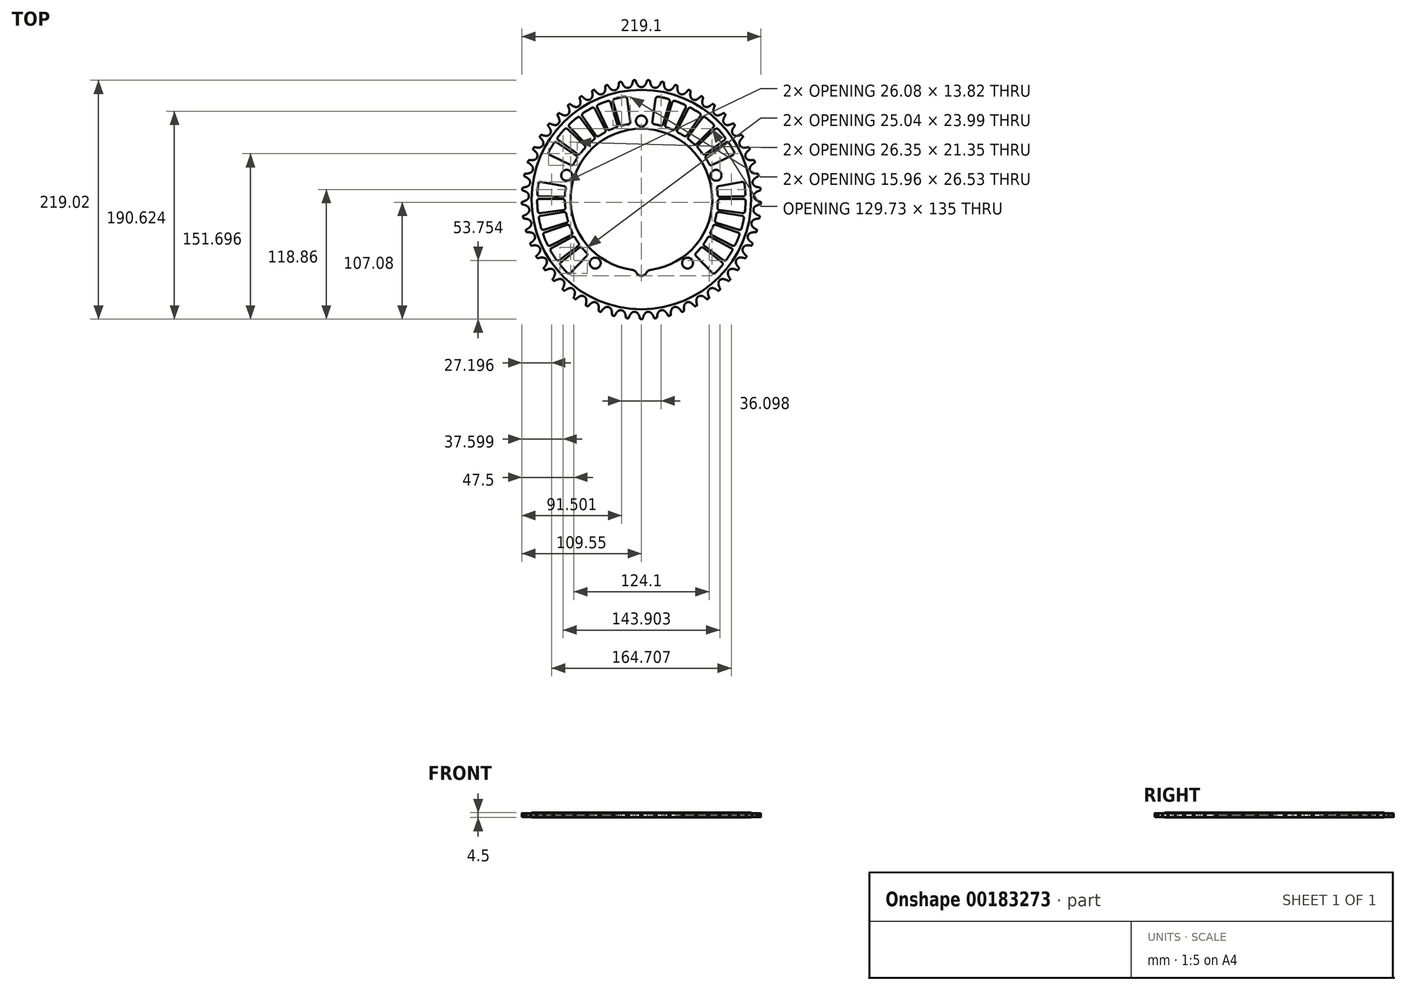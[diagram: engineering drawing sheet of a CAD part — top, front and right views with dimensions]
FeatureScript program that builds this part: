
annotation { "Feature Type Name" : "Feature", "Feature Type Description" : "" }
export const myFeature = defineFeature(function(context is Context, id is Id, definition is map)
    precondition{}
    {
        {
            var Q0;
            Q0=qCreatedBy(makeId("Top.planeOp"),FACE);
            var sketch = newSketch(context, id + "F0", { "sketchPlane" : qUnion([Q0])});
            skArc(sketch, "E0", {"start": v(-4.68, 107.46) * mm, "mid": v(-4.06, 106.06) * mm, "end": v(-3.24, 104.76) * mm});
            skLineSegment(sketch, "E1", {"start": v(-4.68, 107.46) * mm, "end": v(-5.07, 108.57) * mm});
            skArc(sketch, "E2", {"start": v(-5.07, 108.57) * mm, "mid": v(-5.69, 109.87) * mm, "end": v(-6.59, 111) * mm});
            skArc(sketch, "E3.trimOffspring", {"start": v(-3.24, 104.76) * mm, "mid": v(-1.82, 103.55) * mm, "end": v(0, 103.11) * mm});
            skArc(sketch, "E4.MirrorCS", {"start": v(3.24, 104.76) * mm, "mid": v(1.82, 103.55) * mm, "end": v(0, 103.11) * mm});
            skArc(sketch, "E5.MirrorCS", {"start": v(4.68, 107.46) * mm, "mid": v(4.06, 106.06) * mm, "end": v(3.24, 104.76) * mm});
            skLineSegment(sketch, "E6.MirrorCS", {"start": v(4.68, 107.46) * mm, "end": v(5.07, 108.57) * mm});
            skArc(sketch, "E7.MirrorCS", {"start": v(5.07, 108.57) * mm, "mid": v(5.69, 109.87) * mm, "end": v(6.59, 111) * mm});
            skCircle(sketch, "E8", {"center": v(0, 72) * mm, "radius": 5 * mm});
            skCircle(sketch, "E9", {"center": v(0, 0) * mm, "radius": 100.61 * mm});
            skCircle(sketch, "E10", {"center": v(0, 0) * mm, "radius": 65 * mm});
            skCircle(sketch, "E11.1.0", {"center": v(-68.48, 22.25) * mm, "radius": 5 * mm});
            skCircle(sketch, "E11.2.0", {"center": v(-42.32, -58.25) * mm, "radius": 5 * mm});
            skCircle(sketch, "E11.3.0", {"center": v(42.32, -58.25) * mm, "radius": 5 * mm});
            skCircle(sketch, "E11.4.0", {"center": v(68.48, 22.25) * mm, "radius": 5 * mm});
            skCircle(sketch, "E12", {"center": v(0, -65) * mm, "radius": 5 * mm});
            skArc(sketch, "E13.1.0", {"start": v(-17.87, 107.21) * mm, "mid": v(-18.64, 108.43) * mm, "end": v(-19.67, 109.44) * mm});
            skLineSegment(sketch, "E13.1.1", {"start": v(-17.36, 106.15) * mm, "end": v(-17.87, 107.21) * mm});
            skArc(sketch, "E13.1.2", {"start": v(-17.36, 106.15) * mm, "mid": v(-16.58, 104.83) * mm, "end": v(-15.61, 103.64) * mm});
            skArc(sketch, "E13.1.3", {"start": v(-15.61, 103.64) * mm, "mid": v(-14.05, 102.6) * mm, "end": v(-12.2, 102.39) * mm});
            skArc(sketch, "E13.1.4", {"start": v(-9.17, 104.4) * mm, "mid": v(-10.44, 103.04) * mm, "end": v(-12.2, 102.39) * mm});
            skArc(sketch, "E13.1.5", {"start": v(-8.06, 107.26) * mm, "mid": v(-8.51, 105.8) * mm, "end": v(-9.17, 104.4) * mm});
            skLineSegment(sketch, "E13.1.6", {"start": v(-8.06, 107.26) * mm, "end": v(-7.81, 108.4) * mm});
            skArc(sketch, "E13.1.7", {"start": v(-7.81, 108.4) * mm, "mid": v(-7.35, 109.77) * mm, "end": v(-6.59, 111) * mm});
            skArc(sketch, "E13.2.0", {"start": v(-30.43, 104.34) * mm, "mid": v(-31.34, 105.46) * mm, "end": v(-32.47, 106.34) * mm});
            skLineSegment(sketch, "E13.2.1", {"start": v(-29.79, 103.36) * mm, "end": v(-30.43, 104.34) * mm});
            skArc(sketch, "E13.2.2", {"start": v(-29.79, 103.36) * mm, "mid": v(-28.86, 102.14) * mm, "end": v(-27.76, 101.07) * mm});
            skArc(sketch, "E13.2.3", {"start": v(-27.76, 101.07) * mm, "mid": v(-26.09, 100.22) * mm, "end": v(-24.22, 100.23) * mm});
            skArc(sketch, "E13.2.4", {"start": v(-21.45, 102.6) * mm, "mid": v(-22.55, 101.08) * mm, "end": v(-24.22, 100.23) * mm});
            skArc(sketch, "E13.2.5", {"start": v(-20.7, 105.55) * mm, "mid": v(-20.96, 104.04) * mm, "end": v(-21.45, 102.6) * mm});
            skLineSegment(sketch, "E13.2.6", {"start": v(-20.7, 105.55) * mm, "end": v(-20.58, 106.72) * mm});
            skArc(sketch, "E13.2.7", {"start": v(-20.58, 106.72) * mm, "mid": v(-20.28, 108.13) * mm, "end": v(-19.67, 109.44) * mm});
            skArc(sketch, "E13.3.0", {"start": v(-42.55, 100.01) * mm, "mid": v(-43.59, 101.01) * mm, "end": v(-44.82, 101.76) * mm});
            skLineSegment(sketch, "E13.3.1", {"start": v(-41.8, 99.1) * mm, "end": v(-42.55, 100.01) * mm});
            skArc(sketch, "E13.3.2", {"start": v(-41.8, 99.1) * mm, "mid": v(-40.74, 98) * mm, "end": v(-39.52, 97.07) * mm});
            skArc(sketch, "E13.3.3", {"start": v(-39.52, 97.07) * mm, "mid": v(-37.76, 96.43) * mm, "end": v(-35.9, 96.66) * mm});
            skArc(sketch, "E13.3.4", {"start": v(-33.44, 99.33) * mm, "mid": v(-34.35, 97.7) * mm, "end": v(-35.9, 96.66) * mm});
            skArc(sketch, "E13.3.5", {"start": v(-33.03, 102.37) * mm, "mid": v(-33.12, 100.83) * mm, "end": v(-33.44, 99.33) * mm});
            skLineSegment(sketch, "E13.3.6", {"start": v(-33.03, 102.37) * mm, "end": v(-33.06, 103.54) * mm});
            skArc(sketch, "E13.3.7", {"start": v(-33.06, 103.54) * mm, "mid": v(-32.92, 104.98) * mm, "end": v(-32.47, 106.34) * mm});
            skArc(sketch, "E13.4.0", {"start": v(-54.08, 94.28) * mm, "mid": v(-55.23, 95.15) * mm, "end": v(-56.54, 95.74) * mm});
            skLineSegment(sketch, "E13.4.1", {"start": v(-53.23, 93.47) * mm, "end": v(-54.08, 94.28) * mm});
            skArc(sketch, "E13.4.2", {"start": v(-53.23, 93.47) * mm, "mid": v(-52.04, 92.5) * mm, "end": v(-50.72, 91.72) * mm});
            skArc(sketch, "E13.4.3", {"start": v(-50.72, 91.72) * mm, "mid": v(-48.9, 91.3) * mm, "end": v(-47.08, 91.73) * mm});
            skArc(sketch, "E13.4.4", {"start": v(-44.95, 94.68) * mm, "mid": v(-45.66, 92.95) * mm, "end": v(-47.08, 91.73) * mm});
            skArc(sketch, "E13.4.5", {"start": v(-44.9, 97.74) * mm, "mid": v(-44.82, 96.2) * mm, "end": v(-44.95, 94.68) * mm});
            skLineSegment(sketch, "E13.4.6", {"start": v(-44.9, 97.74) * mm, "end": v(-45.07, 98.9) * mm});
            skArc(sketch, "E13.4.7", {"start": v(-45.07, 98.9) * mm, "mid": v(-45.1, 100.34) * mm, "end": v(-44.82, 101.76) * mm});
            skArc(sketch, "E13.5.0", {"start": v(-64.85, 87.22) * mm, "mid": v(-66.1, 87.95) * mm, "end": v(-67.47, 88.38) * mm});
            skLineSegment(sketch, "E13.5.1", {"start": v(-63.91, 86.52) * mm, "end": v(-64.85, 87.22) * mm});
            skArc(sketch, "E13.5.2", {"start": v(-63.91, 86.52) * mm, "mid": v(-62.62, 85.7) * mm, "end": v(-61.21, 85.08) * mm});
            skArc(sketch, "E13.5.3", {"start": v(-61.21, 85.08) * mm, "mid": v(-59.35, 84.87) * mm, "end": v(-57.6, 85.52) * mm});
            skArc(sketch, "E13.5.4", {"start": v(-55.83, 88.7) * mm, "mid": v(-56.34, 86.9) * mm, "end": v(-57.6, 85.52) * mm});
            skArc(sketch, "E13.5.5", {"start": v(-56.15, 91.74) * mm, "mid": v(-55.88, 90.23) * mm, "end": v(-55.83, 88.7) * mm});
            skLineSegment(sketch, "E13.5.6", {"start": v(-56.15, 91.74) * mm, "end": v(-56.45, 92.88) * mm});
            skArc(sketch, "E13.5.7", {"start": v(-56.45, 92.88) * mm, "mid": v(-56.66, 94.3) * mm, "end": v(-56.54, 95.74) * mm});
            skArc(sketch, "E13.6.0", {"start": v(-74.72, 78.94) * mm, "mid": v(-76.04, 79.51) * mm, "end": v(-77.45, 79.78) * mm});
            skLineSegment(sketch, "E13.6.1", {"start": v(-73.7, 78.35) * mm, "end": v(-74.72, 78.94) * mm});
            skArc(sketch, "E13.6.2", {"start": v(-73.7, 78.35) * mm, "mid": v(-72.31, 77.69) * mm, "end": v(-70.85, 77.24) * mm});
            skArc(sketch, "E13.6.3", {"start": v(-70.85, 77.24) * mm, "mid": v(-68.98, 77.25) * mm, "end": v(-67.31, 78.1) * mm});
            skArc(sketch, "E13.6.4", {"start": v(-65.93, 81.47) * mm, "mid": v(-66.22, 79.63) * mm, "end": v(-67.31, 78.1) * mm});
            skArc(sketch, "E13.6.5", {"start": v(-66.6, 84.46) * mm, "mid": v(-66.16, 83) * mm, "end": v(-65.93, 81.47) * mm});
            skLineSegment(sketch, "E13.6.6", {"start": v(-66.6, 84.46) * mm, "end": v(-67.04, 85.55) * mm});
            skArc(sketch, "E13.6.7", {"start": v(-67.04, 85.55) * mm, "mid": v(-67.42, 86.94) * mm, "end": v(-67.47, 88.38) * mm});
            skArc(sketch, "E13.7.0", {"start": v(-83.53, 69.55) * mm, "mid": v(-84.9, 69.96) * mm, "end": v(-86.34, 70.06) * mm});
            skLineSegment(sketch, "E13.7.1", {"start": v(-82.45, 69.08) * mm, "end": v(-83.53, 69.55) * mm});
            skArc(sketch, "E13.7.2", {"start": v(-82.45, 69.08) * mm, "mid": v(-81, 68.6) * mm, "end": v(-79.48, 68.32) * mm});
            skArc(sketch, "E13.7.3", {"start": v(-79.48, 68.32) * mm, "mid": v(-77.63, 68.55) * mm, "end": v(-76.08, 69.6) * mm});
            skArc(sketch, "E13.7.4", {"start": v(-75.1, 73.1) * mm, "mid": v(-75.17, 71.23) * mm, "end": v(-76.08, 69.6) * mm});
            skArc(sketch, "E13.7.5", {"start": v(-76.13, 75.99) * mm, "mid": v(-75.51, 74.58) * mm, "end": v(-75.1, 73.1) * mm});
            skLineSegment(sketch, "E13.7.6", {"start": v(-76.13, 75.99) * mm, "end": v(-76.69, 77.02) * mm});
            skArc(sketch, "E13.7.7", {"start": v(-76.69, 77.02) * mm, "mid": v(-77.23, 78.36) * mm, "end": v(-77.45, 79.78) * mm});
            skArc(sketch, "E13.8.0", {"start": v(-91.17, 59.18) * mm, "mid": v(-92.58, 59.43) * mm, "end": v(-94.02, 59.36) * mm});
            skLineSegment(sketch, "E13.8.1", {"start": v(-90.04, 58.85) * mm, "end": v(-91.17, 59.18) * mm});
            skArc(sketch, "E13.8.2", {"start": v(-90.04, 58.85) * mm, "mid": v(-88.54, 58.53) * mm, "end": v(-87, 58.44) * mm});
            skArc(sketch, "E13.8.3", {"start": v(-87, 58.44) * mm, "mid": v(-85.2, 58.89) * mm, "end": v(-83.78, 60.11) * mm});
            skArc(sketch, "E13.8.4", {"start": v(-83.23, 63.7) * mm, "mid": v(-83.07, 61.84) * mm, "end": v(-83.78, 60.11) * mm});
            skArc(sketch, "E13.8.5", {"start": v(-84.58, 66.45) * mm, "mid": v(-83.8, 65.13) * mm, "end": v(-83.23, 63.7) * mm});
            skLineSegment(sketch, "E13.8.6", {"start": v(-84.58, 66.45) * mm, "end": v(-85.26, 67.41) * mm});
            skArc(sketch, "E13.8.7", {"start": v(-85.26, 67.41) * mm, "mid": v(-85.95, 68.67) * mm, "end": v(-86.34, 70.06) * mm});
            skArc(sketch, "E13.9.0", {"start": v(-97.53, 47.98) * mm, "mid": v(-98.96, 48.06) * mm, "end": v(-100.38, 47.82) * mm});
            skLineSegment(sketch, "E13.9.1", {"start": v(-96.37, 47.78) * mm, "end": v(-97.53, 47.98) * mm});
            skArc(sketch, "E13.9.2", {"start": v(-96.37, 47.78) * mm, "mid": v(-94.84, 47.65) * mm, "end": v(-93.3, 47.74) * mm});
            skArc(sketch, "E13.9.3", {"start": v(-93.3, 47.74) * mm, "mid": v(-91.56, 48.4) * mm, "end": v(-90.3, 49.78) * mm});
            skArc(sketch, "E13.9.4", {"start": v(-90.18, 53.42) * mm, "mid": v(-89.8, 51.58) * mm, "end": v(-90.3, 49.78) * mm});
            skArc(sketch, "E13.9.5", {"start": v(-91.85, 55.98) * mm, "mid": v(-90.92, 54.76) * mm, "end": v(-90.18, 53.42) * mm});
            skLineSegment(sketch, "E13.9.6", {"start": v(-91.85, 55.98) * mm, "end": v(-92.63, 56.85) * mm});
            skArc(sketch, "E13.9.7", {"start": v(-92.63, 56.85) * mm, "mid": v(-93.47, 58.03) * mm, "end": v(-94.02, 59.36) * mm});
            skArc(sketch, "E13.10.0", {"start": v(-102.52, 36.11) * mm, "mid": v(-103.95, 36.02) * mm, "end": v(-105.33, 35.61) * mm});
            skLineSegment(sketch, "E13.10.1", {"start": v(-101.34, 36.05) * mm, "end": v(-102.52, 36.11) * mm});
            skArc(sketch, "E13.10.2", {"start": v(-101.34, 36.05) * mm, "mid": v(-99.8, 36.1) * mm, "end": v(-98.3, 36.37) * mm});
            skArc(sketch, "E13.10.3", {"start": v(-98.3, 36.37) * mm, "mid": v(-96.64, 37.23) * mm, "end": v(-95.55, 38.75) * mm});
            skArc(sketch, "E13.10.4", {"start": v(-95.86, 42.38) * mm, "mid": v(-95.27, 40.6) * mm, "end": v(-95.55, 38.75) * mm});
            skArc(sketch, "E13.10.5", {"start": v(-97.82, 44.72) * mm, "mid": v(-96.76, 43.62) * mm, "end": v(-95.86, 42.38) * mm});
            skLineSegment(sketch, "E13.10.6", {"start": v(-97.82, 44.72) * mm, "end": v(-98.7, 45.5) * mm});
            skArc(sketch, "E13.10.7", {"start": v(-98.7, 45.5) * mm, "mid": v(-99.68, 46.56) * mm, "end": v(-100.38, 47.82) * mm});
            skArc(sketch, "E13.11.0", {"start": v(-106.07, 23.73) * mm, "mid": v(-107.48, 23.47) * mm, "end": v(-108.8, 22.9) * mm});
            skLineSegment(sketch, "E13.11.1", {"start": v(-104.9, 23.81) * mm, "end": v(-106.07, 23.73) * mm});
            skArc(sketch, "E13.11.2", {"start": v(-104.9, 23.81) * mm, "mid": v(-103.38, 24.04) * mm, "end": v(-101.9, 24.49) * mm});
            skArc(sketch, "E13.11.3", {"start": v(-101.9, 24.49) * mm, "mid": v(-100.37, 25.54) * mm, "end": v(-99.47, 27.18) * mm});
            skArc(sketch, "E13.11.4", {"start": v(-100.2, 30.74) * mm, "mid": v(-99.4, 29.05) * mm, "end": v(-99.47, 27.18) * mm});
            skArc(sketch, "E13.11.5", {"start": v(-102.43, 32.84) * mm, "mid": v(-101.24, 31.87) * mm, "end": v(-100.2, 30.74) * mm});
            skLineSegment(sketch, "E13.11.6", {"start": v(-102.43, 32.84) * mm, "end": v(-103.4, 33.5) * mm});
            skArc(sketch, "E13.11.7", {"start": v(-103.4, 33.5) * mm, "mid": v(-104.49, 34.45) * mm, "end": v(-105.33, 35.61) * mm});
            skArc(sketch, "E13.12.0", {"start": v(-108.13, 11.02) * mm, "mid": v(-109.5, 10.6) * mm, "end": v(-110.75, 9.87) * mm});
            skLineSegment(sketch, "E13.12.1", {"start": v(-106.97, 11.24) * mm, "end": v(-108.13, 11.02) * mm});
            skArc(sketch, "E13.12.2", {"start": v(-106.97, 11.24) * mm, "mid": v(-105.5, 11.64) * mm, "end": v(-104.1, 12.26) * mm});
            skArc(sketch, "E13.12.3", {"start": v(-104.1, 12.26) * mm, "mid": v(-102.68, 13.49) * mm, "end": v(-101.98, 15.22) * mm});
            skArc(sketch, "E13.12.4", {"start": v(-103.13, 18.67) * mm, "mid": v(-102.14, 17.09) * mm, "end": v(-101.98, 15.22) * mm});
            skArc(sketch, "E13.12.5", {"start": v(-105.6, 20.5) * mm, "mid": v(-104.3, 19.68) * mm, "end": v(-103.13, 18.67) * mm});
            skLineSegment(sketch, "E13.12.6", {"start": v(-105.6, 20.5) * mm, "end": v(-106.63, 21.04) * mm});
            skArc(sketch, "E13.12.7", {"start": v(-106.63, 21.04) * mm, "mid": v(-107.83, 21.85) * mm, "end": v(-108.8, 22.9) * mm});
            skArc(sketch, "E13.13.0", {"start": v(-108.67, -1.85) * mm, "mid": v(-110, -2.43) * mm, "end": v(-111.14, -3.3) * mm});
            skLineSegment(sketch, "E13.13.1", {"start": v(-107.55, -1.5) * mm, "end": v(-108.67, -1.85) * mm});
            skArc(sketch, "E13.13.2", {"start": v(-107.55, -1.5) * mm, "mid": v(-106.13, -0.92) * mm, "end": v(-104.8, -0.14) * mm});
            skArc(sketch, "E13.13.3", {"start": v(-104.8, -0.14) * mm, "mid": v(-103.56, 1.25) * mm, "end": v(-103.07, 3.06) * mm});
            skArc(sketch, "E13.13.4", {"start": v(-104.62, 6.35) * mm, "mid": v(-103.45, 4.89) * mm, "end": v(-103.07, 3.06) * mm});
            skArc(sketch, "E13.13.5", {"start": v(-107.28, 7.86) * mm, "mid": v(-105.9, 7.2) * mm, "end": v(-104.62, 6.35) * mm});
            skLineSegment(sketch, "E13.13.6", {"start": v(-107.28, 7.86) * mm, "end": v(-108.37, 8.28) * mm});
            skArc(sketch, "E13.13.7", {"start": v(-108.37, 8.28) * mm, "mid": v(-109.65, 8.94) * mm, "end": v(-110.75, 9.87) * mm});
            skArc(sketch, "E13.14.0", {"start": v(-107.7, -14.69) * mm, "mid": v(-108.93, -15.42) * mm, "end": v(-109.97, -16.42) * mm});
            skLineSegment(sketch, "E13.14.1", {"start": v(-106.62, -14.2) * mm, "end": v(-107.7, -14.69) * mm});
            skArc(sketch, "E13.14.2", {"start": v(-106.62, -14.2) * mm, "mid": v(-105.28, -13.46) * mm, "end": v(-104.06, -12.53) * mm});
            skArc(sketch, "E13.14.3", {"start": v(-104.06, -12.53) * mm, "mid": v(-102.98, -11) * mm, "end": v(-102.7, -9.16) * mm});
            skArc(sketch, "E13.14.4", {"start": v(-104.63, -6.07) * mm, "mid": v(-103.3, -7.38) * mm, "end": v(-102.7, -9.16) * mm});
            skArc(sketch, "E13.14.5", {"start": v(-107.45, -4.88) * mm, "mid": v(-106, -5.37) * mm, "end": v(-104.63, -6.07) * mm});
            skLineSegment(sketch, "E13.14.6", {"start": v(-107.45, -4.88) * mm, "end": v(-108.6, -4.6) * mm});
            skArc(sketch, "E13.14.7", {"start": v(-108.6, -4.6) * mm, "mid": v(-109.94, -4.09) * mm, "end": v(-111.14, -3.3) * mm});
            skArc(sketch, "E13.15.0", {"start": v(-105.2, -27.32) * mm, "mid": v(-106.34, -28.2) * mm, "end": v(-107.26, -29.3) * mm});
            skLineSegment(sketch, "E13.15.1", {"start": v(-104.2, -26.71) * mm, "end": v(-105.2, -27.32) * mm});
            skArc(sketch, "E13.15.2", {"start": v(-104.2, -26.71) * mm, "mid": v(-102.95, -25.82) * mm, "end": v(-101.85, -24.75) * mm});
            skArc(sketch, "E13.15.3", {"start": v(-101.85, -24.75) * mm, "mid": v(-100.95, -23.1) * mm, "end": v(-100.9, -21.24) * mm});
            skArc(sketch, "E13.15.4", {"start": v(-103.18, -18.4) * mm, "mid": v(-101.7, -19.55) * mm, "end": v(-100.9, -21.24) * mm});
            skArc(sketch, "E13.15.5", {"start": v(-106.12, -17.56) * mm, "mid": v(-104.62, -17.87) * mm, "end": v(-103.18, -18.4) * mm});
            skLineSegment(sketch, "E13.15.6", {"start": v(-106.12, -17.56) * mm, "end": v(-107.29, -17.4) * mm});
            skArc(sketch, "E13.15.7", {"start": v(-107.29, -17.4) * mm, "mid": v(-108.69, -17.06) * mm, "end": v(-109.97, -16.42) * mm});
            skArc(sketch, "E13.16.0", {"start": v(-101.23, -39.57) * mm, "mid": v(-102.26, -40.58) * mm, "end": v(-103.04, -41.79) * mm});
            skLineSegment(sketch, "E13.16.1", {"start": v(-100.3, -38.85) * mm, "end": v(-101.23, -39.57) * mm});
            skArc(sketch, "E13.16.2", {"start": v(-100.3, -38.85) * mm, "mid": v(-99.17, -37.81) * mm, "end": v(-98.2, -36.62) * mm});
            skArc(sketch, "E13.16.3", {"start": v(-98.2, -36.62) * mm, "mid": v(-97.51, -34.89) * mm, "end": v(-97.68, -33.02) * mm});
            skArc(sketch, "E13.16.4", {"start": v(-100.28, -30.48) * mm, "mid": v(-98.68, -31.44) * mm, "end": v(-97.68, -33.02) * mm});
            skArc(sketch, "E13.16.5", {"start": v(-103.3, -29.98) * mm, "mid": v(-101.77, -30.12) * mm, "end": v(-100.28, -30.48) * mm});
            skLineSegment(sketch, "E13.16.6", {"start": v(-103.3, -29.98) * mm, "end": v(-104.48, -29.97) * mm});
            skArc(sketch, "E13.16.7", {"start": v(-104.48, -29.97) * mm, "mid": v(-105.9, -29.8) * mm, "end": v(-107.26, -29.3) * mm});
            skArc(sketch, "E13.17.0", {"start": v(-95.84, -51.27) * mm, "mid": v(-96.74, -52.39) * mm, "end": v(-97.37, -53.68) * mm});
            skLineSegment(sketch, "E13.17.1", {"start": v(-95, -50.44) * mm, "end": v(-95.84, -51.27) * mm});
            skArc(sketch, "E13.17.2", {"start": v(-95, -50.44) * mm, "mid": v(-94, -49.28) * mm, "end": v(-93.18, -47.98) * mm});
            skArc(sketch, "E13.17.3", {"start": v(-93.18, -47.98) * mm, "mid": v(-92.7, -46.17) * mm, "end": v(-93.09, -44.34) * mm});
            skArc(sketch, "E13.17.4", {"start": v(-95.97, -42.13) * mm, "mid": v(-94.26, -42.9) * mm, "end": v(-93.09, -44.34) * mm});
            skArc(sketch, "E13.17.5", {"start": v(-99.03, -42) * mm, "mid": v(-97.5, -41.95) * mm, "end": v(-95.97, -42.13) * mm});
            skLineSegment(sketch, "E13.17.6", {"start": v(-99.03, -42) * mm, "end": v(-100.2, -42.12) * mm});
            skArc(sketch, "E13.17.7", {"start": v(-100.2, -42.12) * mm, "mid": v(-101.64, -42.12) * mm, "end": v(-103.04, -41.79) * mm});
            skArc(sketch, "E13.18.0", {"start": v(-89.1, -62.24) * mm, "mid": v(-89.87, -63.46) * mm, "end": v(-90.34, -64.82) * mm});
            skLineSegment(sketch, "E13.18.1", {"start": v(-88.37, -61.32) * mm, "end": v(-89.1, -62.24) * mm});
            skArc(sketch, "E13.18.2", {"start": v(-88.37, -61.32) * mm, "mid": v(-87.51, -60.05) * mm, "end": v(-86.85, -58.67) * mm});
            skArc(sketch, "E13.18.3", {"start": v(-86.85, -58.67) * mm, "mid": v(-86.59, -56.81) * mm, "end": v(-87.2, -55.04) * mm});
            skArc(sketch, "E13.18.4", {"start": v(-90.32, -53.18) * mm, "mid": v(-88.53, -53.74) * mm, "end": v(-87.2, -55.04) * mm});
            skArc(sketch, "E13.18.5", {"start": v(-93.37, -53.4) * mm, "mid": v(-91.85, -53.18) * mm, "end": v(-90.32, -53.18) * mm});
            skLineSegment(sketch, "E13.18.6", {"start": v(-93.37, -53.4) * mm, "end": v(-94.51, -53.67) * mm});
            skArc(sketch, "E13.18.7", {"start": v(-94.51, -53.67) * mm, "mid": v(-95.94, -53.84) * mm, "end": v(-97.37, -53.68) * mm});
            skArc(sketch, "E13.19.0", {"start": v(-81.12, -72.34) * mm, "mid": v(-81.73, -73.65) * mm, "end": v(-82.04, -75.05) * mm});
            skLineSegment(sketch, "E13.19.1", {"start": v(-80.5, -71.34) * mm, "end": v(-81.12, -72.34) * mm});
            skArc(sketch, "E13.19.2", {"start": v(-80.5, -71.34) * mm, "mid": v(-79.8, -69.98) * mm, "end": v(-79.3, -68.53) * mm});
            skArc(sketch, "E13.19.3", {"start": v(-79.3, -68.53) * mm, "mid": v(-79.26, -66.66) * mm, "end": v(-80.07, -64.97) * mm});
            skArc(sketch, "E13.19.4", {"start": v(-83.4, -63.49) * mm, "mid": v(-81.55, -63.83) * mm, "end": v(-80.07, -64.97) * mm});
            skArc(sketch, "E13.19.5", {"start": v(-86.4, -64.08) * mm, "mid": v(-84.91, -63.67) * mm, "end": v(-83.4, -63.49) * mm});
            skLineSegment(sketch, "E13.19.6", {"start": v(-86.4, -64.08) * mm, "end": v(-87.5, -64.48) * mm});
            skArc(sketch, "E13.19.7", {"start": v(-87.5, -64.48) * mm, "mid": v(-88.9, -64.81) * mm, "end": v(-90.34, -64.82) * mm});
            skArc(sketch, "E13.20.0", {"start": v(-72, -81.43) * mm, "mid": v(-72.45, -82.8) * mm, "end": v(-72.59, -84.23) * mm});
            skLineSegment(sketch, "E13.20.1", {"start": v(-71.5, -80.36) * mm, "end": v(-72, -81.43) * mm});
            skArc(sketch, "E13.20.2", {"start": v(-71.5, -80.36) * mm, "mid": v(-70.96, -78.93) * mm, "end": v(-70.64, -77.42) * mm});
            skArc(sketch, "E13.20.3", {"start": v(-70.64, -77.42) * mm, "mid": v(-70.82, -75.56) * mm, "end": v(-71.82, -73.98) * mm});
            skArc(sketch, "E13.20.4", {"start": v(-75.3, -72.9) * mm, "mid": v(-73.43, -73.03) * mm, "end": v(-71.82, -73.98) * mm});
            skArc(sketch, "E13.20.5", {"start": v(-78.2, -73.85) * mm, "mid": v(-76.79, -73.27) * mm, "end": v(-75.3, -72.9) * mm});
            skLineSegment(sketch, "E13.20.6", {"start": v(-78.2, -73.85) * mm, "end": v(-79.26, -74.37) * mm});
            skArc(sketch, "E13.20.7", {"start": v(-79.26, -74.37) * mm, "mid": v(-80.61, -74.87) * mm, "end": v(-82.04, -75.05) * mm});
            skArc(sketch, "E13.21.0", {"start": v(-61.86, -89.37) * mm, "mid": v(-62.15, -90.78) * mm, "end": v(-62.12, -92.22) * mm});
            skLineSegment(sketch, "E13.21.1", {"start": v(-61.49, -88.26) * mm, "end": v(-61.86, -89.37) * mm});
            skArc(sketch, "E13.21.2", {"start": v(-61.49, -88.26) * mm, "mid": v(-61.13, -86.76) * mm, "end": v(-61, -85.24) * mm});
            skArc(sketch, "E13.21.3", {"start": v(-61, -85.24) * mm, "mid": v(-61.39, -83.4) * mm, "end": v(-62.57, -81.96) * mm});
            skArc(sketch, "E13.21.4", {"start": v(-66.15, -81.3) * mm, "mid": v(-64.28, -81.2) * mm, "end": v(-62.57, -81.96) * mm});
            skArc(sketch, "E13.21.5", {"start": v(-68.93, -82.58) * mm, "mid": v(-67.58, -81.84) * mm, "end": v(-66.15, -81.3) * mm});
            skLineSegment(sketch, "E13.21.6", {"start": v(-68.93, -82.58) * mm, "end": v(-69.9, -83.23) * mm});
            skArc(sketch, "E13.21.7", {"start": v(-69.9, -83.23) * mm, "mid": v(-71.2, -83.88) * mm, "end": v(-72.59, -84.23) * mm});
            skArc(sketch, "E13.22.0", {"start": v(-50.85, -96.06) * mm, "mid": v(-50.97, -97.5) * mm, "end": v(-50.77, -98.92) * mm});
            skLineSegment(sketch, "E13.22.1", {"start": v(-50.62, -94.9) * mm, "end": v(-50.85, -96.06) * mm});
            skArc(sketch, "E13.22.2", {"start": v(-50.62, -94.9) * mm, "mid": v(-50.44, -93.39) * mm, "end": v(-50.48, -91.85) * mm});
            skArc(sketch, "E13.22.3", {"start": v(-50.48, -91.85) * mm, "mid": v(-51.1, -90.08) * mm, "end": v(-52.44, -88.78) * mm});
            skArc(sketch, "E13.22.4", {"start": v(-56.07, -88.55) * mm, "mid": v(-54.22, -88.23) * mm, "end": v(-52.44, -88.78) * mm});
            skArc(sketch, "E13.22.5", {"start": v(-58.68, -90.15) * mm, "mid": v(-57.43, -89.25) * mm, "end": v(-56.07, -88.55) * mm});
            skLineSegment(sketch, "E13.22.6", {"start": v(-58.68, -90.15) * mm, "end": v(-59.57, -90.9) * mm});
            skArc(sketch, "E13.22.7", {"start": v(-59.57, -90.9) * mm, "mid": v(-60.77, -91.71) * mm, "end": v(-62.12, -92.22) * mm});
            skArc(sketch, "E13.23.0", {"start": v(-39.13, -101.4) * mm, "mid": v(-39.09, -102.84) * mm, "end": v(-38.72, -104.23) * mm});
            skLineSegment(sketch, "E13.23.1", {"start": v(-39.04, -100.23) * mm, "end": v(-39.13, -101.4) * mm});
            skArc(sketch, "E13.23.2", {"start": v(-39.04, -100.23) * mm, "mid": v(-39.04, -98.7) * mm, "end": v(-39.26, -97.18) * mm});
            skArc(sketch, "E13.23.3", {"start": v(-39.26, -97.18) * mm, "mid": v(-40.08, -95.5) * mm, "end": v(-41.57, -94.36) * mm});
            skArc(sketch, "E13.23.4", {"start": v(-45.2, -94.56) * mm, "mid": v(-43.4, -94.03) * mm, "end": v(-41.57, -94.36) * mm});
            skArc(sketch, "E13.23.5", {"start": v(-47.6, -96.46) * mm, "mid": v(-46.47, -95.42) * mm, "end": v(-45.2, -94.56) * mm});
            skLineSegment(sketch, "E13.23.6", {"start": v(-47.6, -96.46) * mm, "end": v(-48.4, -97.32) * mm});
            skArc(sketch, "E13.23.7", {"start": v(-48.4, -97.32) * mm, "mid": v(-49.5, -98.25) * mm, "end": v(-50.77, -98.92) * mm});
            skArc(sketch, "E13.24.0", {"start": v(-26.86, -105.32) * mm, "mid": v(-26.65, -106.74) * mm, "end": v(-26.12, -108.08) * mm});
            skLineSegment(sketch, "E13.24.1", {"start": v(-26.9, -104.14) * mm, "end": v(-26.86, -105.32) * mm});
            skArc(sketch, "E13.24.2", {"start": v(-26.9, -104.14) * mm, "mid": v(-27.1, -102.62) * mm, "end": v(-27.5, -101.14) * mm});
            skArc(sketch, "E13.24.3", {"start": v(-27.5, -101.14) * mm, "mid": v(-28.5, -99.56) * mm, "end": v(-30.11, -98.62) * mm});
            skArc(sketch, "E13.24.4", {"start": v(-33.7, -99.25) * mm, "mid": v(-31.98, -98.5) * mm, "end": v(-30.11, -98.62) * mm});
            skArc(sketch, "E13.24.5", {"start": v(-35.86, -101.4) * mm, "mid": v(-34.86, -100.25) * mm, "end": v(-33.7, -99.25) * mm});
            skLineSegment(sketch, "E13.24.6", {"start": v(-35.86, -101.4) * mm, "end": v(-36.55, -102.36) * mm});
            skArc(sketch, "E13.24.7", {"start": v(-36.55, -102.36) * mm, "mid": v(-37.53, -103.42) * mm, "end": v(-38.72, -104.23) * mm});
            skArc(sketch, "E13.25.0", {"start": v(-14.22, -107.76) * mm, "mid": v(-13.84, -109.14) * mm, "end": v(-13.15, -110.41) * mm});
            skLineSegment(sketch, "E13.25.1", {"start": v(-14.4, -106.6) * mm, "end": v(-14.22, -107.76) * mm});
            skArc(sketch, "E13.25.2", {"start": v(-14.4, -106.6) * mm, "mid": v(-14.76, -105.1) * mm, "end": v(-15.34, -103.68) * mm});
            skArc(sketch, "E13.25.3", {"start": v(-15.34, -103.68) * mm, "mid": v(-16.53, -102.24) * mm, "end": v(-18.24, -101.49) * mm});
            skArc(sketch, "E13.25.4", {"start": v(-21.72, -102.53) * mm, "mid": v(-20.1, -101.6) * mm, "end": v(-18.24, -101.49) * mm});
            skArc(sketch, "E13.25.5", {"start": v(-23.61, -104.94) * mm, "mid": v(-22.76, -103.67) * mm, "end": v(-21.72, -102.53) * mm});
            skLineSegment(sketch, "E13.25.6", {"start": v(-23.61, -104.94) * mm, "end": v(-24.2, -105.96) * mm});
            skArc(sketch, "E13.25.7", {"start": v(-24.2, -105.96) * mm, "mid": v(-25.03, -107.13) * mm, "end": v(-26.12, -108.08) * mm});
            skArc(sketch, "E13.26.0", {"start": v(-1.38, -108.68) * mm, "mid": v(-0.83, -110.01) * mm, "end": v(0, -111.2) * mm});
            skLineSegment(sketch, "E13.26.1", {"start": v(-1.7, -107.55) * mm, "end": v(-1.38, -108.68) * mm});
            skArc(sketch, "E13.26.2", {"start": v(-1.7, -107.55) * mm, "mid": v(-2.23, -106.11) * mm, "end": v(-2.97, -104.77) * mm});
            skArc(sketch, "E13.26.3", {"start": v(-2.97, -104.77) * mm, "mid": v(-4.32, -103.47) * mm, "end": v(-6.1, -102.93) * mm});
            skArc(sketch, "E13.26.4", {"start": v(-9.44, -104.38) * mm, "mid": v(-7.95, -103.26) * mm, "end": v(-6.1, -102.93) * mm});
            skArc(sketch, "E13.26.5", {"start": v(-11.04, -107) * mm, "mid": v(-10.34, -105.63) * mm, "end": v(-9.44, -104.38) * mm});
            skLineSegment(sketch, "E13.26.6", {"start": v(-11.04, -107) * mm, "end": v(-11.49, -108.08) * mm});
            skArc(sketch, "E13.26.7", {"start": v(-11.49, -108.08) * mm, "mid": v(-12.19, -109.34) * mm, "end": v(-13.15, -110.41) * mm});
            skArc(sketch, "E13.27.0", {"start": v(11.49, -108.08) * mm, "mid": v(12.19, -109.34) * mm, "end": v(13.15, -110.41) * mm});
            skLineSegment(sketch, "E13.27.1", {"start": v(11.04, -107) * mm, "end": v(11.49, -108.08) * mm});
            skArc(sketch, "E13.27.2", {"start": v(11.04, -107) * mm, "mid": v(10.34, -105.63) * mm, "end": v(9.44, -104.38) * mm});
            skArc(sketch, "E13.27.3", {"start": v(9.44, -104.38) * mm, "mid": v(7.95, -103.26) * mm, "end": v(6.1, -102.93) * mm});
            skArc(sketch, "E13.27.4", {"start": v(2.97, -104.77) * mm, "mid": v(4.32, -103.47) * mm, "end": v(6.1, -102.93) * mm});
            skArc(sketch, "E13.27.5", {"start": v(1.7, -107.55) * mm, "mid": v(2.23, -106.11) * mm, "end": v(2.97, -104.77) * mm});
            skLineSegment(sketch, "E13.27.6", {"start": v(1.7, -107.55) * mm, "end": v(1.38, -108.68) * mm});
            skArc(sketch, "E13.27.7", {"start": v(1.38, -108.68) * mm, "mid": v(0.83, -110.01) * mm, "end": v(0, -111.2) * mm});
            skArc(sketch, "E13.28.0", {"start": v(24.2, -105.96) * mm, "mid": v(25.03, -107.13) * mm, "end": v(26.12, -108.08) * mm});
            skLineSegment(sketch, "E13.28.1", {"start": v(23.61, -104.94) * mm, "end": v(24.2, -105.96) * mm});
            skArc(sketch, "E13.28.2", {"start": v(23.61, -104.94) * mm, "mid": v(22.76, -103.67) * mm, "end": v(21.72, -102.53) * mm});
            skArc(sketch, "E13.28.3", {"start": v(21.72, -102.53) * mm, "mid": v(20.1, -101.6) * mm, "end": v(18.24, -101.49) * mm});
            skArc(sketch, "E13.28.4", {"start": v(15.34, -103.68) * mm, "mid": v(16.53, -102.24) * mm, "end": v(18.24, -101.49) * mm});
            skArc(sketch, "E13.28.5", {"start": v(14.4, -106.6) * mm, "mid": v(14.76, -105.1) * mm, "end": v(15.34, -103.68) * mm});
            skLineSegment(sketch, "E13.28.6", {"start": v(14.4, -106.6) * mm, "end": v(14.22, -107.76) * mm});
            skArc(sketch, "E13.28.7", {"start": v(14.22, -107.76) * mm, "mid": v(13.84, -109.14) * mm, "end": v(13.15, -110.41) * mm});
            skArc(sketch, "E13.29.0", {"start": v(36.55, -102.36) * mm, "mid": v(37.53, -103.42) * mm, "end": v(38.72, -104.23) * mm});
            skLineSegment(sketch, "E13.29.1", {"start": v(35.86, -101.4) * mm, "end": v(36.55, -102.36) * mm});
            skArc(sketch, "E13.29.2", {"start": v(35.86, -101.4) * mm, "mid": v(34.86, -100.25) * mm, "end": v(33.7, -99.25) * mm});
            skArc(sketch, "E13.29.3", {"start": v(33.7, -99.25) * mm, "mid": v(31.98, -98.5) * mm, "end": v(30.11, -98.62) * mm});
            skArc(sketch, "E13.29.4", {"start": v(27.5, -101.14) * mm, "mid": v(28.5, -99.56) * mm, "end": v(30.11, -98.62) * mm});
            skArc(sketch, "E13.29.5", {"start": v(26.9, -104.14) * mm, "mid": v(27.1, -102.62) * mm, "end": v(27.5, -101.14) * mm});
            skLineSegment(sketch, "E13.29.6", {"start": v(26.9, -104.14) * mm, "end": v(26.86, -105.32) * mm});
            skArc(sketch, "E13.29.7", {"start": v(26.86, -105.32) * mm, "mid": v(26.65, -106.74) * mm, "end": v(26.12, -108.08) * mm});
            skArc(sketch, "E13.30.0", {"start": v(48.4, -97.32) * mm, "mid": v(49.5, -98.25) * mm, "end": v(50.77, -98.92) * mm});
            skLineSegment(sketch, "E13.30.1", {"start": v(47.6, -96.46) * mm, "end": v(48.4, -97.32) * mm});
            skArc(sketch, "E13.30.2", {"start": v(47.6, -96.46) * mm, "mid": v(46.47, -95.42) * mm, "end": v(45.2, -94.56) * mm});
            skArc(sketch, "E13.30.3", {"start": v(45.2, -94.56) * mm, "mid": v(43.4, -94.03) * mm, "end": v(41.57, -94.36) * mm});
            skArc(sketch, "E13.30.4", {"start": v(39.26, -97.18) * mm, "mid": v(40.08, -95.5) * mm, "end": v(41.57, -94.36) * mm});
            skArc(sketch, "E13.30.5", {"start": v(39.04, -100.23) * mm, "mid": v(39.04, -98.7) * mm, "end": v(39.26, -97.18) * mm});
            skLineSegment(sketch, "E13.30.6", {"start": v(39.04, -100.23) * mm, "end": v(39.13, -101.4) * mm});
            skArc(sketch, "E13.30.7", {"start": v(39.13, -101.4) * mm, "mid": v(39.09, -102.84) * mm, "end": v(38.72, -104.23) * mm});
            skArc(sketch, "E13.31.0", {"start": v(59.57, -90.9) * mm, "mid": v(60.77, -91.71) * mm, "end": v(62.12, -92.22) * mm});
            skLineSegment(sketch, "E13.31.1", {"start": v(58.68, -90.15) * mm, "end": v(59.57, -90.9) * mm});
            skArc(sketch, "E13.31.2", {"start": v(58.68, -90.15) * mm, "mid": v(57.43, -89.25) * mm, "end": v(56.07, -88.55) * mm});
            skArc(sketch, "E13.31.3", {"start": v(56.07, -88.55) * mm, "mid": v(54.22, -88.23) * mm, "end": v(52.44, -88.78) * mm});
            skArc(sketch, "E13.31.4", {"start": v(50.48, -91.85) * mm, "mid": v(51.1, -90.08) * mm, "end": v(52.44, -88.78) * mm});
            skArc(sketch, "E13.31.5", {"start": v(50.62, -94.9) * mm, "mid": v(50.44, -93.39) * mm, "end": v(50.48, -91.85) * mm});
            skLineSegment(sketch, "E13.31.6", {"start": v(50.62, -94.9) * mm, "end": v(50.85, -96.06) * mm});
            skArc(sketch, "E13.31.7", {"start": v(50.85, -96.06) * mm, "mid": v(50.97, -97.5) * mm, "end": v(50.77, -98.92) * mm});
            skArc(sketch, "E13.32.0", {"start": v(69.9, -83.23) * mm, "mid": v(71.2, -83.88) * mm, "end": v(72.59, -84.23) * mm});
            skLineSegment(sketch, "E13.32.1", {"start": v(68.93, -82.58) * mm, "end": v(69.9, -83.23) * mm});
            skArc(sketch, "E13.32.2", {"start": v(68.93, -82.58) * mm, "mid": v(67.58, -81.84) * mm, "end": v(66.15, -81.3) * mm});
            skArc(sketch, "E13.32.3", {"start": v(66.15, -81.3) * mm, "mid": v(64.28, -81.2) * mm, "end": v(62.57, -81.96) * mm});
            skArc(sketch, "E13.32.4", {"start": v(61, -85.24) * mm, "mid": v(61.39, -83.4) * mm, "end": v(62.57, -81.96) * mm});
            skArc(sketch, "E13.32.5", {"start": v(61.49, -88.26) * mm, "mid": v(61.13, -86.76) * mm, "end": v(61, -85.24) * mm});
            skLineSegment(sketch, "E13.32.6", {"start": v(61.49, -88.26) * mm, "end": v(61.86, -89.37) * mm});
            skArc(sketch, "E13.32.7", {"start": v(61.86, -89.37) * mm, "mid": v(62.15, -90.78) * mm, "end": v(62.12, -92.22) * mm});
            skArc(sketch, "E13.33.0", {"start": v(79.26, -74.37) * mm, "mid": v(80.61, -74.87) * mm, "end": v(82.04, -75.05) * mm});
            skLineSegment(sketch, "E13.33.1", {"start": v(78.2, -73.85) * mm, "end": v(79.26, -74.37) * mm});
            skArc(sketch, "E13.33.2", {"start": v(78.2, -73.85) * mm, "mid": v(76.79, -73.27) * mm, "end": v(75.3, -72.9) * mm});
            skArc(sketch, "E13.33.3", {"start": v(75.3, -72.9) * mm, "mid": v(73.43, -73.03) * mm, "end": v(71.82, -73.98) * mm});
            skArc(sketch, "E13.33.4", {"start": v(70.64, -77.42) * mm, "mid": v(70.82, -75.56) * mm, "end": v(71.82, -73.98) * mm});
            skArc(sketch, "E13.33.5", {"start": v(71.5, -80.36) * mm, "mid": v(70.96, -78.93) * mm, "end": v(70.64, -77.42) * mm});
            skLineSegment(sketch, "E13.33.6", {"start": v(71.5, -80.36) * mm, "end": v(72, -81.43) * mm});
            skArc(sketch, "E13.33.7", {"start": v(72, -81.43) * mm, "mid": v(72.45, -82.8) * mm, "end": v(72.59, -84.23) * mm});
            skArc(sketch, "E13.34.0", {"start": v(87.5, -64.48) * mm, "mid": v(88.9, -64.81) * mm, "end": v(90.34, -64.82) * mm});
            skLineSegment(sketch, "E13.34.1", {"start": v(86.4, -64.08) * mm, "end": v(87.5, -64.48) * mm});
            skArc(sketch, "E13.34.2", {"start": v(86.4, -64.08) * mm, "mid": v(84.91, -63.67) * mm, "end": v(83.4, -63.49) * mm});
            skArc(sketch, "E13.34.3", {"start": v(83.4, -63.49) * mm, "mid": v(81.55, -63.83) * mm, "end": v(80.07, -64.97) * mm});
            skArc(sketch, "E13.34.4", {"start": v(79.3, -68.53) * mm, "mid": v(79.26, -66.66) * mm, "end": v(80.07, -64.97) * mm});
            skArc(sketch, "E13.34.5", {"start": v(80.5, -71.34) * mm, "mid": v(79.8, -69.98) * mm, "end": v(79.3, -68.53) * mm});
            skLineSegment(sketch, "E13.34.6", {"start": v(80.5, -71.34) * mm, "end": v(81.12, -72.34) * mm});
            skArc(sketch, "E13.34.7", {"start": v(81.12, -72.34) * mm, "mid": v(81.73, -73.65) * mm, "end": v(82.04, -75.05) * mm});
            skArc(sketch, "E13.35.0", {"start": v(94.51, -53.67) * mm, "mid": v(95.94, -53.84) * mm, "end": v(97.37, -53.68) * mm});
            skLineSegment(sketch, "E13.35.1", {"start": v(93.37, -53.4) * mm, "end": v(94.51, -53.67) * mm});
            skArc(sketch, "E13.35.2", {"start": v(93.37, -53.4) * mm, "mid": v(91.85, -53.18) * mm, "end": v(90.32, -53.18) * mm});
            skArc(sketch, "E13.35.3", {"start": v(90.32, -53.18) * mm, "mid": v(88.53, -53.74) * mm, "end": v(87.2, -55.04) * mm});
            skArc(sketch, "E13.35.4", {"start": v(86.85, -58.67) * mm, "mid": v(86.59, -56.81) * mm, "end": v(87.2, -55.04) * mm});
            skArc(sketch, "E13.35.5", {"start": v(88.37, -61.32) * mm, "mid": v(87.51, -60.05) * mm, "end": v(86.85, -58.67) * mm});
            skLineSegment(sketch, "E13.35.6", {"start": v(88.37, -61.32) * mm, "end": v(89.1, -62.24) * mm});
            skArc(sketch, "E13.35.7", {"start": v(89.1, -62.24) * mm, "mid": v(89.87, -63.46) * mm, "end": v(90.34, -64.82) * mm});
            skArc(sketch, "E13.36.0", {"start": v(100.2, -42.12) * mm, "mid": v(101.64, -42.12) * mm, "end": v(103.04, -41.79) * mm});
            skLineSegment(sketch, "E13.36.1", {"start": v(99.03, -42) * mm, "end": v(100.2, -42.12) * mm});
            skArc(sketch, "E13.36.2", {"start": v(99.03, -42) * mm, "mid": v(97.5, -41.95) * mm, "end": v(95.97, -42.13) * mm});
            skArc(sketch, "E13.36.3", {"start": v(95.97, -42.13) * mm, "mid": v(94.26, -42.9) * mm, "end": v(93.09, -44.34) * mm});
            skArc(sketch, "E13.36.4", {"start": v(93.18, -47.98) * mm, "mid": v(92.7, -46.17) * mm, "end": v(93.09, -44.34) * mm});
            skArc(sketch, "E13.36.5", {"start": v(95, -50.44) * mm, "mid": v(94, -49.28) * mm, "end": v(93.18, -47.98) * mm});
            skLineSegment(sketch, "E13.36.6", {"start": v(95, -50.44) * mm, "end": v(95.84, -51.27) * mm});
            skArc(sketch, "E13.36.7", {"start": v(95.84, -51.27) * mm, "mid": v(96.74, -52.39) * mm, "end": v(97.37, -53.68) * mm});
            skArc(sketch, "E13.37.0", {"start": v(104.48, -29.97) * mm, "mid": v(105.9, -29.8) * mm, "end": v(107.26, -29.3) * mm});
            skLineSegment(sketch, "E13.37.1", {"start": v(103.3, -29.98) * mm, "end": v(104.48, -29.97) * mm});
            skArc(sketch, "E13.37.2", {"start": v(103.3, -29.98) * mm, "mid": v(101.77, -30.12) * mm, "end": v(100.28, -30.48) * mm});
            skArc(sketch, "E13.37.3", {"start": v(100.28, -30.48) * mm, "mid": v(98.68, -31.44) * mm, "end": v(97.68, -33.02) * mm});
            skArc(sketch, "E13.37.4", {"start": v(98.2, -36.62) * mm, "mid": v(97.51, -34.89) * mm, "end": v(97.68, -33.02) * mm});
            skArc(sketch, "E13.37.5", {"start": v(100.3, -38.85) * mm, "mid": v(99.17, -37.81) * mm, "end": v(98.2, -36.62) * mm});
            skLineSegment(sketch, "E13.37.6", {"start": v(100.3, -38.85) * mm, "end": v(101.23, -39.57) * mm});
            skArc(sketch, "E13.37.7", {"start": v(101.23, -39.57) * mm, "mid": v(102.26, -40.58) * mm, "end": v(103.04, -41.79) * mm});
            skArc(sketch, "E13.38.0", {"start": v(107.29, -17.4) * mm, "mid": v(108.69, -17.06) * mm, "end": v(109.97, -16.42) * mm});
            skLineSegment(sketch, "E13.38.1", {"start": v(106.12, -17.56) * mm, "end": v(107.29, -17.4) * mm});
            skArc(sketch, "E13.38.2", {"start": v(106.12, -17.56) * mm, "mid": v(104.62, -17.87) * mm, "end": v(103.18, -18.4) * mm});
            skArc(sketch, "E13.38.3", {"start": v(103.18, -18.4) * mm, "mid": v(101.7, -19.55) * mm, "end": v(100.9, -21.24) * mm});
            skArc(sketch, "E13.38.4", {"start": v(101.85, -24.75) * mm, "mid": v(100.95, -23.1) * mm, "end": v(100.9, -21.24) * mm});
            skArc(sketch, "E13.38.5", {"start": v(104.2, -26.71) * mm, "mid": v(102.95, -25.82) * mm, "end": v(101.85, -24.75) * mm});
            skLineSegment(sketch, "E13.38.6", {"start": v(104.2, -26.71) * mm, "end": v(105.2, -27.32) * mm});
            skArc(sketch, "E13.38.7", {"start": v(105.2, -27.32) * mm, "mid": v(106.34, -28.2) * mm, "end": v(107.26, -29.3) * mm});
            skArc(sketch, "E13.39.0", {"start": v(108.6, -4.6) * mm, "mid": v(109.94, -4.09) * mm, "end": v(111.14, -3.3) * mm});
            skLineSegment(sketch, "E13.39.1", {"start": v(107.45, -4.88) * mm, "end": v(108.6, -4.6) * mm});
            skArc(sketch, "E13.39.2", {"start": v(107.45, -4.88) * mm, "mid": v(106, -5.37) * mm, "end": v(104.63, -6.07) * mm});
            skArc(sketch, "E13.39.3", {"start": v(104.63, -6.07) * mm, "mid": v(103.3, -7.38) * mm, "end": v(102.7, -9.16) * mm});
            skArc(sketch, "E13.39.4", {"start": v(104.06, -12.53) * mm, "mid": v(102.98, -11) * mm, "end": v(102.7, -9.16) * mm});
            skArc(sketch, "E13.39.5", {"start": v(106.62, -14.2) * mm, "mid": v(105.28, -13.46) * mm, "end": v(104.06, -12.53) * mm});
            skLineSegment(sketch, "E13.39.6", {"start": v(106.62, -14.2) * mm, "end": v(107.7, -14.69) * mm});
            skArc(sketch, "E13.39.7", {"start": v(107.7, -14.69) * mm, "mid": v(108.93, -15.42) * mm, "end": v(109.97, -16.42) * mm});
            skArc(sketch, "E13.40.0", {"start": v(108.37, 8.28) * mm, "mid": v(109.65, 8.94) * mm, "end": v(110.75, 9.87) * mm});
            skLineSegment(sketch, "E13.40.1", {"start": v(107.28, 7.86) * mm, "end": v(108.37, 8.28) * mm});
            skArc(sketch, "E13.40.2", {"start": v(107.28, 7.86) * mm, "mid": v(105.9, 7.2) * mm, "end": v(104.62, 6.35) * mm});
            skArc(sketch, "E13.40.3", {"start": v(104.62, 6.35) * mm, "mid": v(103.45, 4.89) * mm, "end": v(103.07, 3.06) * mm});
            skArc(sketch, "E13.40.4", {"start": v(104.8, -0.14) * mm, "mid": v(103.56, 1.25) * mm, "end": v(103.07, 3.06) * mm});
            skArc(sketch, "E13.40.5", {"start": v(107.55, -1.5) * mm, "mid": v(106.13, -0.92) * mm, "end": v(104.8, -0.14) * mm});
            skLineSegment(sketch, "E13.40.6", {"start": v(107.55, -1.5) * mm, "end": v(108.67, -1.85) * mm});
            skArc(sketch, "E13.40.7", {"start": v(108.67, -1.85) * mm, "mid": v(110, -2.43) * mm, "end": v(111.14, -3.3) * mm});
            skArc(sketch, "E13.41.0", {"start": v(106.63, 21.04) * mm, "mid": v(107.83, 21.85) * mm, "end": v(108.8, 22.9) * mm});
            skLineSegment(sketch, "E13.41.1", {"start": v(105.6, 20.5) * mm, "end": v(106.63, 21.04) * mm});
            skArc(sketch, "E13.41.2", {"start": v(105.6, 20.5) * mm, "mid": v(104.3, 19.68) * mm, "end": v(103.13, 18.67) * mm});
            skArc(sketch, "E13.41.3", {"start": v(103.13, 18.67) * mm, "mid": v(102.14, 17.09) * mm, "end": v(101.98, 15.22) * mm});
            skArc(sketch, "E13.41.4", {"start": v(104.1, 12.26) * mm, "mid": v(102.68, 13.49) * mm, "end": v(101.98, 15.22) * mm});
            skArc(sketch, "E13.41.5", {"start": v(106.97, 11.24) * mm, "mid": v(105.5, 11.64) * mm, "end": v(104.1, 12.26) * mm});
            skLineSegment(sketch, "E13.41.6", {"start": v(106.97, 11.24) * mm, "end": v(108.13, 11.02) * mm});
            skArc(sketch, "E13.41.7", {"start": v(108.13, 11.02) * mm, "mid": v(109.5, 10.6) * mm, "end": v(110.75, 9.87) * mm});
            skArc(sketch, "E13.42.0", {"start": v(103.4, 33.5) * mm, "mid": v(104.49, 34.45) * mm, "end": v(105.33, 35.61) * mm});
            skLineSegment(sketch, "E13.42.1", {"start": v(102.43, 32.84) * mm, "end": v(103.4, 33.5) * mm});
            skArc(sketch, "E13.42.2", {"start": v(102.43, 32.84) * mm, "mid": v(101.24, 31.87) * mm, "end": v(100.2, 30.74) * mm});
            skArc(sketch, "E13.42.3", {"start": v(100.2, 30.74) * mm, "mid": v(99.4, 29.05) * mm, "end": v(99.47, 27.18) * mm});
            skArc(sketch, "E13.42.4", {"start": v(101.9, 24.49) * mm, "mid": v(100.37, 25.54) * mm, "end": v(99.47, 27.18) * mm});
            skArc(sketch, "E13.42.5", {"start": v(104.9, 23.81) * mm, "mid": v(103.38, 24.04) * mm, "end": v(101.9, 24.49) * mm});
            skLineSegment(sketch, "E13.42.6", {"start": v(104.9, 23.81) * mm, "end": v(106.07, 23.73) * mm});
            skArc(sketch, "E13.42.7", {"start": v(106.07, 23.73) * mm, "mid": v(107.48, 23.47) * mm, "end": v(108.8, 22.9) * mm});
            skArc(sketch, "E13.43.0", {"start": v(98.7, 45.5) * mm, "mid": v(99.68, 46.56) * mm, "end": v(100.38, 47.82) * mm});
            skLineSegment(sketch, "E13.43.1", {"start": v(97.82, 44.72) * mm, "end": v(98.7, 45.5) * mm});
            skArc(sketch, "E13.43.2", {"start": v(97.82, 44.72) * mm, "mid": v(96.76, 43.62) * mm, "end": v(95.86, 42.38) * mm});
            skArc(sketch, "E13.43.3", {"start": v(95.86, 42.38) * mm, "mid": v(95.27, 40.6) * mm, "end": v(95.55, 38.75) * mm});
            skArc(sketch, "E13.43.4", {"start": v(98.3, 36.37) * mm, "mid": v(96.64, 37.23) * mm, "end": v(95.55, 38.75) * mm});
            skArc(sketch, "E13.43.5", {"start": v(101.34, 36.05) * mm, "mid": v(99.8, 36.1) * mm, "end": v(98.3, 36.37) * mm});
            skLineSegment(sketch, "E13.43.6", {"start": v(101.34, 36.05) * mm, "end": v(102.52, 36.11) * mm});
            skArc(sketch, "E13.43.7", {"start": v(102.52, 36.11) * mm, "mid": v(103.95, 36.02) * mm, "end": v(105.33, 35.61) * mm});
            skArc(sketch, "E13.44.0", {"start": v(92.63, 56.85) * mm, "mid": v(93.47, 58.03) * mm, "end": v(94.02, 59.36) * mm});
            skLineSegment(sketch, "E13.44.1", {"start": v(91.85, 55.98) * mm, "end": v(92.63, 56.85) * mm});
            skArc(sketch, "E13.44.2", {"start": v(91.85, 55.98) * mm, "mid": v(90.92, 54.76) * mm, "end": v(90.18, 53.42) * mm});
            skArc(sketch, "E13.44.3", {"start": v(90.18, 53.42) * mm, "mid": v(89.8, 51.58) * mm, "end": v(90.3, 49.78) * mm});
            skArc(sketch, "E13.44.4", {"start": v(93.3, 47.74) * mm, "mid": v(91.56, 48.4) * mm, "end": v(90.3, 49.78) * mm});
            skArc(sketch, "E13.44.5", {"start": v(96.37, 47.78) * mm, "mid": v(94.84, 47.65) * mm, "end": v(93.3, 47.74) * mm});
            skLineSegment(sketch, "E13.44.6", {"start": v(96.37, 47.78) * mm, "end": v(97.53, 47.98) * mm});
            skArc(sketch, "E13.44.7", {"start": v(97.53, 47.98) * mm, "mid": v(98.96, 48.06) * mm, "end": v(100.38, 47.82) * mm});
            skArc(sketch, "E13.45.0", {"start": v(85.26, 67.41) * mm, "mid": v(85.95, 68.67) * mm, "end": v(86.34, 70.06) * mm});
            skLineSegment(sketch, "E13.45.1", {"start": v(84.58, 66.45) * mm, "end": v(85.26, 67.41) * mm});
            skArc(sketch, "E13.45.2", {"start": v(84.58, 66.45) * mm, "mid": v(83.8, 65.13) * mm, "end": v(83.23, 63.7) * mm});
            skArc(sketch, "E13.45.3", {"start": v(83.23, 63.7) * mm, "mid": v(83.07, 61.84) * mm, "end": v(83.78, 60.11) * mm});
            skArc(sketch, "E13.45.4", {"start": v(87, 58.44) * mm, "mid": v(85.2, 58.89) * mm, "end": v(83.78, 60.11) * mm});
            skArc(sketch, "E13.45.5", {"start": v(90.04, 58.85) * mm, "mid": v(88.54, 58.53) * mm, "end": v(87, 58.44) * mm});
            skLineSegment(sketch, "E13.45.6", {"start": v(90.04, 58.85) * mm, "end": v(91.17, 59.18) * mm});
            skArc(sketch, "E13.45.7", {"start": v(91.17, 59.18) * mm, "mid": v(92.58, 59.43) * mm, "end": v(94.02, 59.36) * mm});
            skArc(sketch, "E13.46.0", {"start": v(76.69, 77.02) * mm, "mid": v(77.23, 78.36) * mm, "end": v(77.45, 79.78) * mm});
            skLineSegment(sketch, "E13.46.1", {"start": v(76.13, 75.99) * mm, "end": v(76.69, 77.02) * mm});
            skArc(sketch, "E13.46.2", {"start": v(76.13, 75.99) * mm, "mid": v(75.51, 74.58) * mm, "end": v(75.1, 73.1) * mm});
            skArc(sketch, "E13.46.3", {"start": v(75.1, 73.1) * mm, "mid": v(75.17, 71.23) * mm, "end": v(76.08, 69.6) * mm});
            skArc(sketch, "E13.46.4", {"start": v(79.48, 68.32) * mm, "mid": v(77.63, 68.55) * mm, "end": v(76.08, 69.6) * mm});
            skArc(sketch, "E13.46.5", {"start": v(82.45, 69.08) * mm, "mid": v(81, 68.6) * mm, "end": v(79.48, 68.32) * mm});
            skLineSegment(sketch, "E13.46.6", {"start": v(82.45, 69.08) * mm, "end": v(83.53, 69.55) * mm});
            skArc(sketch, "E13.46.7", {"start": v(83.53, 69.55) * mm, "mid": v(84.9, 69.96) * mm, "end": v(86.34, 70.06) * mm});
            skArc(sketch, "E13.47.0", {"start": v(67.04, 85.55) * mm, "mid": v(67.42, 86.94) * mm, "end": v(67.47, 88.38) * mm});
            skLineSegment(sketch, "E13.47.1", {"start": v(66.6, 84.46) * mm, "end": v(67.04, 85.55) * mm});
            skArc(sketch, "E13.47.2", {"start": v(66.6, 84.46) * mm, "mid": v(66.16, 83) * mm, "end": v(65.93, 81.47) * mm});
            skArc(sketch, "E13.47.3", {"start": v(65.93, 81.47) * mm, "mid": v(66.22, 79.63) * mm, "end": v(67.31, 78.1) * mm});
            skArc(sketch, "E13.47.4", {"start": v(70.85, 77.24) * mm, "mid": v(68.98, 77.25) * mm, "end": v(67.31, 78.1) * mm});
            skArc(sketch, "E13.47.5", {"start": v(73.7, 78.35) * mm, "mid": v(72.31, 77.69) * mm, "end": v(70.85, 77.24) * mm});
            skLineSegment(sketch, "E13.47.6", {"start": v(73.7, 78.35) * mm, "end": v(74.72, 78.94) * mm});
            skArc(sketch, "E13.47.7", {"start": v(74.72, 78.94) * mm, "mid": v(76.04, 79.51) * mm, "end": v(77.45, 79.78) * mm});
            skArc(sketch, "E13.48.0", {"start": v(56.45, 92.88) * mm, "mid": v(56.66, 94.3) * mm, "end": v(56.54, 95.74) * mm});
            skLineSegment(sketch, "E13.48.1", {"start": v(56.15, 91.74) * mm, "end": v(56.45, 92.88) * mm});
            skArc(sketch, "E13.48.2", {"start": v(56.15, 91.74) * mm, "mid": v(55.88, 90.23) * mm, "end": v(55.83, 88.7) * mm});
            skArc(sketch, "E13.48.3", {"start": v(55.83, 88.7) * mm, "mid": v(56.34, 86.9) * mm, "end": v(57.6, 85.52) * mm});
            skArc(sketch, "E13.48.4", {"start": v(61.21, 85.08) * mm, "mid": v(59.35, 84.87) * mm, "end": v(57.6, 85.52) * mm});
            skArc(sketch, "E13.48.5", {"start": v(63.91, 86.52) * mm, "mid": v(62.62, 85.7) * mm, "end": v(61.21, 85.08) * mm});
            skLineSegment(sketch, "E13.48.6", {"start": v(63.91, 86.52) * mm, "end": v(64.85, 87.22) * mm});
            skArc(sketch, "E13.48.7", {"start": v(64.85, 87.22) * mm, "mid": v(66.1, 87.95) * mm, "end": v(67.47, 88.38) * mm});
            skArc(sketch, "E13.49.0", {"start": v(45.07, 98.9) * mm, "mid": v(45.1, 100.34) * mm, "end": v(44.82, 101.76) * mm});
            skLineSegment(sketch, "E13.49.1", {"start": v(44.9, 97.74) * mm, "end": v(45.07, 98.9) * mm});
            skArc(sketch, "E13.49.2", {"start": v(44.9, 97.74) * mm, "mid": v(44.82, 96.2) * mm, "end": v(44.95, 94.68) * mm});
            skArc(sketch, "E13.49.3", {"start": v(44.95, 94.68) * mm, "mid": v(45.66, 92.95) * mm, "end": v(47.08, 91.73) * mm});
            skArc(sketch, "E13.49.4", {"start": v(50.72, 91.72) * mm, "mid": v(48.9, 91.3) * mm, "end": v(47.08, 91.73) * mm});
            skArc(sketch, "E13.49.5", {"start": v(53.23, 93.47) * mm, "mid": v(52.04, 92.5) * mm, "end": v(50.72, 91.72) * mm});
            skLineSegment(sketch, "E13.49.6", {"start": v(53.23, 93.47) * mm, "end": v(54.08, 94.28) * mm});
            skArc(sketch, "E13.49.7", {"start": v(54.08, 94.28) * mm, "mid": v(55.23, 95.15) * mm, "end": v(56.54, 95.74) * mm});
            skArc(sketch, "E13.50.0", {"start": v(33.06, 103.54) * mm, "mid": v(32.92, 104.98) * mm, "end": v(32.47, 106.34) * mm});
            skLineSegment(sketch, "E13.50.1", {"start": v(33.03, 102.37) * mm, "end": v(33.06, 103.54) * mm});
            skArc(sketch, "E13.50.2", {"start": v(33.03, 102.37) * mm, "mid": v(33.12, 100.83) * mm, "end": v(33.44, 99.33) * mm});
            skArc(sketch, "E13.50.3", {"start": v(33.44, 99.33) * mm, "mid": v(34.35, 97.7) * mm, "end": v(35.9, 96.66) * mm});
            skArc(sketch, "E13.50.4", {"start": v(39.52, 97.07) * mm, "mid": v(37.76, 96.43) * mm, "end": v(35.9, 96.66) * mm});
            skArc(sketch, "E13.50.5", {"start": v(41.8, 99.1) * mm, "mid": v(40.74, 98) * mm, "end": v(39.52, 97.07) * mm});
            skLineSegment(sketch, "E13.50.6", {"start": v(41.8, 99.1) * mm, "end": v(42.55, 100.01) * mm});
            skArc(sketch, "E13.50.7", {"start": v(42.55, 100.01) * mm, "mid": v(43.59, 101.01) * mm, "end": v(44.82, 101.76) * mm});
            skArc(sketch, "E13.51.0", {"start": v(20.58, 106.72) * mm, "mid": v(20.28, 108.13) * mm, "end": v(19.67, 109.44) * mm});
            skLineSegment(sketch, "E13.51.1", {"start": v(20.7, 105.55) * mm, "end": v(20.58, 106.72) * mm});
            skArc(sketch, "E13.51.2", {"start": v(20.7, 105.55) * mm, "mid": v(20.96, 104.04) * mm, "end": v(21.45, 102.6) * mm});
            skArc(sketch, "E13.51.3", {"start": v(21.45, 102.6) * mm, "mid": v(22.55, 101.08) * mm, "end": v(24.22, 100.23) * mm});
            skArc(sketch, "E13.51.4", {"start": v(27.76, 101.07) * mm, "mid": v(26.09, 100.22) * mm, "end": v(24.22, 100.23) * mm});
            skArc(sketch, "E13.51.5", {"start": v(29.79, 103.36) * mm, "mid": v(28.86, 102.14) * mm, "end": v(27.76, 101.07) * mm});
            skLineSegment(sketch, "E13.51.6", {"start": v(29.79, 103.36) * mm, "end": v(30.43, 104.34) * mm});
            skArc(sketch, "E13.51.7", {"start": v(30.43, 104.34) * mm, "mid": v(31.34, 105.46) * mm, "end": v(32.47, 106.34) * mm});
            skArc(sketch, "E13.52.0", {"start": v(7.81, 108.4) * mm, "mid": v(7.35, 109.77) * mm, "end": v(6.59, 111) * mm});
            skLineSegment(sketch, "E13.52.1", {"start": v(8.06, 107.26) * mm, "end": v(7.81, 108.4) * mm});
            skArc(sketch, "E13.52.2", {"start": v(8.06, 107.26) * mm, "mid": v(8.51, 105.8) * mm, "end": v(9.17, 104.4) * mm});
            skArc(sketch, "E13.52.3", {"start": v(9.17, 104.4) * mm, "mid": v(10.44, 103.04) * mm, "end": v(12.2, 102.39) * mm});
            skArc(sketch, "E13.52.4", {"start": v(15.61, 103.64) * mm, "mid": v(14.05, 102.6) * mm, "end": v(12.2, 102.39) * mm});
            skArc(sketch, "E13.52.5", {"start": v(17.36, 106.15) * mm, "mid": v(16.58, 104.83) * mm, "end": v(15.61, 103.64) * mm});
            skLineSegment(sketch, "E13.52.6", {"start": v(17.36, 106.15) * mm, "end": v(17.87, 107.21) * mm});
            skArc(sketch, "E13.52.7", {"start": v(17.87, 107.21) * mm, "mid": v(18.64, 108.43) * mm, "end": v(19.67, 109.44) * mm});
            skCircle(sketch, "E14", {"center": v(0, 0) * mm, "radius": 109.58 * mm});
            skLineSegment(sketch, "E15", {"start": v(0, 0) * mm, "end": v(-68.48, 22.25) * mm, "construction": true});
            skSolve(sketch);
        }
        {
            var Q0;
            Q0=makeQuery(id+"F0.imprint","IMPRINT",FACE,{"disambiguationData":[TD([[makeQuery(id+"F0.imprint","IMPRINT",EDGE,{"derivedFrom":sQuery(id+"F0.wireOp",EDGE,"E0")}),-1.0]])]});
            extrude(context, id + "F1", {"entities" : qUnion([Q0]), "endBound" : BoundingType.SYMMETRIC, "depth" : 3.5 * mm});
        }
        {
            var Q0;
            Q0=makeQuery(id+"F0.imprint","IMPRINT",FACE,{"disambiguationData":[TD([[makeQuery(id+"F0.imprint","IMPRINT",EDGE,{"derivedFrom":sQuery(id+"F0.wireOp",EDGE,"E8")}),-1.0]])]});
            extrude(context, id + "F2", {"entities" : qUnion([Q0]), "operationType" : NewBodyOperationType.ADD, "endBound" : BoundingType.SYMMETRIC, "depth" : 4.5 * mm});
        }
        {
            var Q0;
            {var subQ0=sQuery(id+"F0.wireOp",EDGE,"E12");var subQ1=sQuery(id+"F0.wireOp",EDGE,"E10");Q0=makeQuery(id+"F2.opExtrude","SWEPT_EDGE",EDGE,{"disambiguationData":[OSD([subQ1,subQ0]),TDD([makeQuery(id+"F0.imprint","INTERSECT",VERTEX,{"disambiguationData":[OD(1.0)],"derivedFrom":[subQ1,subQ0]})])]});}
            var Q1;
            {var subQ0=sQuery(id+"F0.wireOp",EDGE,"E12");var subQ1=sQuery(id+"F0.wireOp",EDGE,"E10");Q1=makeQuery(id+"F2.opExtrude","SWEPT_EDGE",EDGE,{"disambiguationData":[OSD([subQ1,subQ0]),TDD([makeQuery(id+"F0.imprint","INTERSECT",VERTEX,{"disambiguationData":[OD(0.0)],"derivedFrom":[subQ1,subQ0]})])]});}
            fillet(context, id + "F3", {"entities" : qUnion([Q0, Q1]), "radius" : 5.08 * mm, "tangentPropagation" : true, "allowEdgeOverflow" : false});
        }
        {
            var Q0;
            Q0=makeQuery(id+"F2.opExtrude","CAP_FACE",FACE,{"disambiguationData":[OSD([sQuery(id+"F0.wireOp",EDGE,"E8"),sQuery(id+"F0.wireOp",EDGE,"E9"),sQuery(id+"F0.wireOp",EDGE,"E10"),sQuery(id+"F0.wireOp",EDGE,"E11.1.0"),sQuery(id+"F0.wireOp",EDGE,"E11.2.0"),sQuery(id+"F0.wireOp",EDGE,"E11.3.0"),sQuery(id+"F0.wireOp",EDGE,"E11.4.0"),sQuery(id+"F0.wireOp",EDGE,"E12")])],"isStart":false});
            var sketch = newSketch(context, id + "F4", { "sketchPlane" : qUnion([Q0])});
            skArc(sketch, "E16", {"start": v(48.72, -50.37) * mm, "mid": v(52.15, -46.82) * mm, "end": v(55.31, -43.03) * mm});
            skArc(sketch, "E17", {"start": v(66.42, -68.66) * mm, "mid": v(71.09, -63.82) * mm, "end": v(75.4, -58.66) * mm});
            skLineSegment(sketch, "E18", {"start": v(69.03, 12.11) * mm, "end": v(94.1, 16.51) * mm});
            skLineSegment(sketch, "E19", {"start": v(48.72, -50.37) * mm, "end": v(66.42, -68.66) * mm});
            skLineSegment(sketch, "E20", {"start": v(70.04, 2.3) * mm, "end": v(95.48, 3.14) * mm});
            skLineSegment(sketch, "E21", {"start": v(70.08, 0.47) * mm, "end": v(95.53, 0.64) * mm});
            skLineSegment(sketch, "E22", {"start": v(69.45, -9.37) * mm, "end": v(94.67, -12.77) * mm});
            skLineSegment(sketch, "E23", {"start": v(69.18, -11.18) * mm, "end": v(94.3, -15.25) * mm});
            skLineSegment(sketch, "E24", {"start": v(66.93, -20.78) * mm, "end": v(91.23, -28.33) * mm});
            skLineSegment(sketch, "E25", {"start": v(66.36, -22.53) * mm, "end": v(90.46, -30.7) * mm});
            skLineSegment(sketch, "E26", {"start": v(62.54, -31.62) * mm, "end": v(85.26, -43.1) * mm});
            skLineSegment(sketch, "E27", {"start": v(61.7, -33.24) * mm, "end": v(84.1, -45.32) * mm});
            skLineSegment(sketch, "E28", {"start": v(56.42, -41.57) * mm, "end": v(76.9, -56.67) * mm});
            skLineSegment(sketch, "E29", {"start": v(55.31, -43.03) * mm, "end": v(75.4, -58.66) * mm});
            skArc(sketch, "E30.trimOffspring", {"start": v(95.48, 3.14) * mm, "mid": v(95.02, 9.85) * mm, "end": v(94.1, 16.51) * mm});
            skArc(sketch, "E31.trimOffspring", {"start": v(70.04, 2.3) * mm, "mid": v(69.7, 7.23) * mm, "end": v(69.03, 12.11) * mm});
            skArc(sketch, "E32.trimOffspring", {"start": v(69.45, -9.37) * mm, "mid": v(69.94, -4.46) * mm, "end": v(70.08, 0.47) * mm});
            skArc(sketch, "E33.trimOffspring", {"start": v(94.67, -12.77) * mm, "mid": v(95.34, -6.08) * mm, "end": v(95.53, 0.64) * mm});
            skArc(sketch, "E34.trimOffspring", {"start": v(91.23, -28.33) * mm, "mid": v(93, -21.84) * mm, "end": v(94.3, -15.25) * mm});
            skArc(sketch, "E35.trimOffspring", {"start": v(76.9, -56.67) * mm, "mid": v(80.7, -51.12) * mm, "end": v(84.1, -45.32) * mm});
            skArc(sketch, "E36.trimOffspring", {"start": v(85.26, -43.1) * mm, "mid": v(88.08, -37) * mm, "end": v(90.46, -30.7) * mm});
            skArc(sketch, "E37.trimOffspring", {"start": v(66.93, -20.78) * mm, "mid": v(68.22, -16.02) * mm, "end": v(69.18, -11.18) * mm});
            skArc(sketch, "E38.trimOffspring", {"start": v(62.54, -31.62) * mm, "mid": v(64.61, -27.14) * mm, "end": v(66.36, -22.53) * mm});
            skArc(sketch, "E39.trimOffspring", {"start": v(56.42, -41.57) * mm, "mid": v(59.2, -37.5) * mm, "end": v(61.7, -33.24) * mm});
            skLineSegment(sketch, "E40.1.0", {"start": v(62.96, 30.77) * mm, "end": v(85.83, 41.95) * mm});
            skArc(sketch, "E40.1.1", {"start": v(85.83, 41.95) * mm, "mid": v(82.67, 47.88) * mm, "end": v(79.1, 53.58) * mm});
            skLineSegment(sketch, "E40.1.2", {"start": v(50.68, 48.4) * mm, "end": v(69.09, 65.98) * mm});
            skArc(sketch, "E40.1.3", {"start": v(30.37, 63.16) * mm, "mid": v(25.85, 65.14) * mm, "end": v(21.2, 66.8) * mm});
            skArc(sketch, "E40.1.4", {"start": v(19.45, 67.33) * mm, "mid": v(14.67, 68.53) * mm, "end": v(9.81, 69.39) * mm});
            skLineSegment(sketch, "E40.1.5", {"start": v(19.45, 67.33) * mm, "end": v(26.52, 91.78) * mm});
            skLineSegment(sketch, "E40.1.6", {"start": v(32.01, 62.34) * mm, "end": v(43.64, 84.98) * mm});
            skArc(sketch, "E40.1.7", {"start": v(62.96, 30.77) * mm, "mid": v(60.64, 35.13) * mm, "end": v(58.02, 39.3) * mm});
            skLineSegment(sketch, "E40.1.8", {"start": v(9.81, 69.39) * mm, "end": v(13.37, 94.6) * mm});
            skLineSegment(sketch, "E40.1.9", {"start": v(30.37, 63.16) * mm, "end": v(41.4, 86.1) * mm});
            skLineSegment(sketch, "E40.1.10", {"start": v(21.2, 66.8) * mm, "end": v(28.91, 91.05) * mm});
            skArc(sketch, "E40.1.11", {"start": v(26.52, 91.78) * mm, "mid": v(20, 93.42) * mm, "end": v(13.37, 94.6) * mm});
            skLineSegment(sketch, "E40.1.12", {"start": v(58.02, 39.3) * mm, "end": v(79.1, 53.58) * mm});
            skLineSegment(sketch, "E40.1.13", {"start": v(40.45, 57.23) * mm, "end": v(55.14, 78.02) * mm});
            skLineSegment(sketch, "E40.1.14", {"start": v(41.93, 56.15) * mm, "end": v(57.16, 76.55) * mm});
            skArc(sketch, "E40.1.15", {"start": v(67.34, 67.77) * mm, "mid": v(62.4, 72.34) * mm, "end": v(57.16, 76.55) * mm});
            skLineSegment(sketch, "E40.1.16", {"start": v(49.4, 49.71) * mm, "end": v(67.34, 67.77) * mm});
            skArc(sketch, "E40.1.17", {"start": v(77.66, 55.63) * mm, "mid": v(73.56, 60.96) * mm, "end": v(69.09, 65.98) * mm});
            skLineSegment(sketch, "E40.1.18", {"start": v(56.97, 40.81) * mm, "end": v(77.66, 55.63) * mm});
            skArc(sketch, "E40.1.19", {"start": v(41.4, 86.1) * mm, "mid": v(35.24, 88.8) * mm, "end": v(28.91, 91.05) * mm});
            skArc(sketch, "E40.1.20", {"start": v(55.14, 78.02) * mm, "mid": v(49.51, 81.7) * mm, "end": v(43.64, 84.98) * mm});
            skArc(sketch, "E40.1.21", {"start": v(40.45, 57.23) * mm, "mid": v(36.32, 59.93) * mm, "end": v(32.01, 62.34) * mm});
            skArc(sketch, "E40.1.22", {"start": v(56.97, 40.81) * mm, "mid": v(53.96, 44.72) * mm, "end": v(50.68, 48.4) * mm});
            skArc(sketch, "E40.1.23", {"start": v(49.4, 49.71) * mm, "mid": v(45.78, 53.06) * mm, "end": v(41.93, 56.15) * mm});
            skLineSegment(sketch, "E40.2.0", {"start": v(-9.81, 69.39) * mm, "end": v(-13.37, 94.6) * mm});
            skArc(sketch, "E40.2.1", {"start": v(-13.37, 94.6) * mm, "mid": v(-20, 93.42) * mm, "end": v(-26.52, 91.78) * mm});
            skLineSegment(sketch, "E40.2.2", {"start": v(-30.37, 63.16) * mm, "end": v(-41.4, 86.1) * mm});
            skArc(sketch, "E40.2.3", {"start": v(-50.68, 48.4) * mm, "mid": v(-53.96, 44.72) * mm, "end": v(-56.97, 40.81) * mm});
            skArc(sketch, "E40.2.4", {"start": v(-58.02, 39.3) * mm, "mid": v(-60.64, 35.13) * mm, "end": v(-62.96, 30.77) * mm});
            skLineSegment(sketch, "E40.2.5", {"start": v(-58.02, 39.3) * mm, "end": v(-79.1, 53.58) * mm});
            skLineSegment(sketch, "E40.2.6", {"start": v(-49.4, 49.71) * mm, "end": v(-67.34, 67.77) * mm});
            skArc(sketch, "E40.2.7", {"start": v(-9.81, 69.39) * mm, "mid": v(-14.67, 68.53) * mm, "end": v(-19.45, 67.33) * mm});
            skLineSegment(sketch, "E40.2.8", {"start": v(-62.96, 30.77) * mm, "end": v(-85.83, 41.95) * mm});
            skLineSegment(sketch, "E40.2.9", {"start": v(-50.68, 48.4) * mm, "end": v(-69.09, 65.98) * mm});
            skLineSegment(sketch, "E40.2.10", {"start": v(-56.97, 40.81) * mm, "end": v(-77.66, 55.63) * mm});
            skArc(sketch, "E40.2.11", {"start": v(-79.1, 53.58) * mm, "mid": v(-82.67, 47.88) * mm, "end": v(-85.83, 41.95) * mm});
            skLineSegment(sketch, "E40.2.12", {"start": v(-19.45, 67.33) * mm, "end": v(-26.52, 91.78) * mm});
            skLineSegment(sketch, "E40.2.13", {"start": v(-41.93, 56.15) * mm, "end": v(-57.16, 76.55) * mm});
            skLineSegment(sketch, "E40.2.14", {"start": v(-40.45, 57.23) * mm, "end": v(-55.14, 78.02) * mm});
            skArc(sketch, "E40.2.15", {"start": v(-43.64, 84.98) * mm, "mid": v(-49.51, 81.7) * mm, "end": v(-55.14, 78.02) * mm});
            skLineSegment(sketch, "E40.2.16", {"start": v(-32.01, 62.34) * mm, "end": v(-43.64, 84.98) * mm});
            skArc(sketch, "E40.2.17", {"start": v(-28.91, 91.05) * mm, "mid": v(-35.24, 88.8) * mm, "end": v(-41.4, 86.1) * mm});
            skLineSegment(sketch, "E40.2.18", {"start": v(-21.2, 66.8) * mm, "end": v(-28.91, 91.05) * mm});
            skArc(sketch, "E40.2.19", {"start": v(-69.09, 65.98) * mm, "mid": v(-73.56, 60.96) * mm, "end": v(-77.66, 55.63) * mm});
            skArc(sketch, "E40.2.20", {"start": v(-57.16, 76.55) * mm, "mid": v(-62.4, 72.34) * mm, "end": v(-67.34, 67.77) * mm});
            skArc(sketch, "E40.2.21", {"start": v(-41.93, 56.15) * mm, "mid": v(-45.78, 53.06) * mm, "end": v(-49.4, 49.71) * mm});
            skArc(sketch, "E40.2.22", {"start": v(-21.2, 66.8) * mm, "mid": v(-25.85, 65.14) * mm, "end": v(-30.37, 63.16) * mm});
            skArc(sketch, "E40.2.23", {"start": v(-32.01, 62.34) * mm, "mid": v(-36.32, 59.93) * mm, "end": v(-40.45, 57.23) * mm});
            skLineSegment(sketch, "E40.3.0", {"start": v(-69.03, 12.11) * mm, "end": v(-94.1, 16.51) * mm});
            skArc(sketch, "E40.3.1", {"start": v(-94.1, 16.51) * mm, "mid": v(-95.02, 9.85) * mm, "end": v(-95.48, 3.14) * mm});
            skLineSegment(sketch, "E40.3.2", {"start": v(-69.45, -9.37) * mm, "end": v(-94.67, -12.77) * mm});
            skArc(sketch, "E40.3.3", {"start": v(-61.7, -33.24) * mm, "mid": v(-59.2, -37.5) * mm, "end": v(-56.42, -41.57) * mm});
            skArc(sketch, "E40.3.4", {"start": v(-55.31, -43.03) * mm, "mid": v(-52.15, -46.82) * mm, "end": v(-48.72, -50.37) * mm});
            skLineSegment(sketch, "E40.3.5", {"start": v(-55.31, -43.03) * mm, "end": v(-75.4, -58.66) * mm});
            skLineSegment(sketch, "E40.3.6", {"start": v(-62.54, -31.62) * mm, "end": v(-85.26, -43.1) * mm});
            skArc(sketch, "E40.3.7", {"start": v(-69.03, 12.11) * mm, "mid": v(-69.7, 7.23) * mm, "end": v(-70.04, 2.3) * mm});
            skLineSegment(sketch, "E40.3.8", {"start": v(-48.72, -50.37) * mm, "end": v(-66.42, -68.66) * mm});
            skLineSegment(sketch, "E40.3.9", {"start": v(-61.7, -33.24) * mm, "end": v(-84.1, -45.32) * mm});
            skLineSegment(sketch, "E40.3.10", {"start": v(-56.42, -41.57) * mm, "end": v(-76.9, -56.67) * mm});
            skArc(sketch, "E40.3.11", {"start": v(-75.4, -58.66) * mm, "mid": v(-71.09, -63.82) * mm, "end": v(-66.42, -68.66) * mm});
            skLineSegment(sketch, "E40.3.12", {"start": v(-70.04, 2.3) * mm, "end": v(-95.48, 3.14) * mm});
            skLineSegment(sketch, "E40.3.13", {"start": v(-66.36, -22.53) * mm, "end": v(-90.46, -30.7) * mm});
            skLineSegment(sketch, "E40.3.14", {"start": v(-66.93, -20.78) * mm, "end": v(-91.23, -28.33) * mm});
            skArc(sketch, "E40.3.15", {"start": v(-94.3, -15.25) * mm, "mid": v(-93, -21.84) * mm, "end": v(-91.23, -28.33) * mm});
            skLineSegment(sketch, "E40.3.16", {"start": v(-69.18, -11.18) * mm, "end": v(-94.3, -15.25) * mm});
            skArc(sketch, "E40.3.17", {"start": v(-95.53, 0.64) * mm, "mid": v(-95.34, -6.08) * mm, "end": v(-94.67, -12.77) * mm});
            skLineSegment(sketch, "E40.3.18", {"start": v(-70.08, 0.47) * mm, "end": v(-95.53, 0.64) * mm});
            skArc(sketch, "E40.3.19", {"start": v(-84.1, -45.32) * mm, "mid": v(-80.7, -51.12) * mm, "end": v(-76.9, -56.67) * mm});
            skArc(sketch, "E40.3.20", {"start": v(-90.46, -30.7) * mm, "mid": v(-88.08, -37) * mm, "end": v(-85.26, -43.1) * mm});
            skArc(sketch, "E40.3.21", {"start": v(-66.36, -22.53) * mm, "mid": v(-64.61, -27.14) * mm, "end": v(-62.54, -31.62) * mm});
            skArc(sketch, "E40.3.22", {"start": v(-70.08, 0.47) * mm, "mid": v(-69.94, -4.46) * mm, "end": v(-69.45, -9.37) * mm});
            skArc(sketch, "E40.3.23", {"start": v(-69.18, -11.18) * mm, "mid": v(-68.22, -16.02) * mm, "end": v(-66.93, -20.78) * mm});
            skSolve(sketch);
        }
        {
            var Q0;
            Q0=makeQuery(id+"F4.imprint","IMPRINT",FACE,{"disambiguationData":[TD([[makeQuery(id+"F4.imprint","IMPRINT",EDGE,{"derivedFrom":sQuery(id+"F4.wireOp",EDGE,"E40.3.4")}),-1.0]])]});
            var Q1;
            Q1=makeQuery(id+"F4.imprint","IMPRINT",FACE,{"disambiguationData":[TD([[makeQuery(id+"F4.imprint","IMPRINT",EDGE,{"derivedFrom":sQuery(id+"F4.wireOp",EDGE,"E40.3.3")}),-1.0]])]});
            var Q2;
            Q2=makeQuery(id+"F4.imprint","IMPRINT",FACE,{"disambiguationData":[TD([[makeQuery(id+"F4.imprint","IMPRINT",EDGE,{"derivedFrom":sQuery(id+"F4.wireOp",EDGE,"E40.3.14")}),-1.0]])]});
            var Q3;
            Q3=makeQuery(id+"F4.imprint","IMPRINT",FACE,{"disambiguationData":[TD([[makeQuery(id+"F4.imprint","IMPRINT",EDGE,{"derivedFrom":sQuery(id+"F4.wireOp",EDGE,"E40.3.0")}),1.0]])]});
            var Q4;
            Q4=makeQuery(id+"F4.imprint","IMPRINT",FACE,{"disambiguationData":[TD([[makeQuery(id+"F4.imprint","IMPRINT",EDGE,{"derivedFrom":sQuery(id+"F4.wireOp",EDGE,"E40.2.4")}),-1.0]])]});
            var Q5;
            Q5=makeQuery(id+"F4.imprint","IMPRINT",FACE,{"disambiguationData":[TD([[makeQuery(id+"F4.imprint","IMPRINT",EDGE,{"derivedFrom":sQuery(id+"F4.wireOp",EDGE,"E40.2.3")}),-1.0]])]});
            var Q6;
            Q6=makeQuery(id+"F4.imprint","IMPRINT",FACE,{"disambiguationData":[TD([[makeQuery(id+"F4.imprint","IMPRINT",EDGE,{"derivedFrom":sQuery(id+"F4.wireOp",EDGE,"E40.2.14")}),-1.0]])]});
            var Q7;
            Q7=makeQuery(id+"F4.imprint","IMPRINT",FACE,{"disambiguationData":[TD([[makeQuery(id+"F4.imprint","IMPRINT",EDGE,{"derivedFrom":sQuery(id+"F4.wireOp",EDGE,"E40.2.0")}),1.0]])]});
            var Q8;
            Q8=makeQuery(id+"F4.imprint","IMPRINT",FACE,{"disambiguationData":[TD([[makeQuery(id+"F4.imprint","IMPRINT",EDGE,{"derivedFrom":sQuery(id+"F4.wireOp",EDGE,"E40.1.4")}),-1.0]])]});
            var Q9;
            Q9=makeQuery(id+"F4.imprint","IMPRINT",FACE,{"disambiguationData":[TD([[makeQuery(id+"F4.imprint","IMPRINT",EDGE,{"derivedFrom":sQuery(id+"F4.wireOp",EDGE,"E40.1.3")}),-1.0]])]});
            var Q10;
            Q10=makeQuery(id+"F4.imprint","IMPRINT",FACE,{"disambiguationData":[TD([[makeQuery(id+"F4.imprint","IMPRINT",EDGE,{"derivedFrom":sQuery(id+"F4.wireOp",EDGE,"E40.1.14")}),-1.0]])]});
            var Q11;
            Q11=makeQuery(id+"F4.imprint","IMPRINT",FACE,{"disambiguationData":[TD([[makeQuery(id+"F4.imprint","IMPRINT",EDGE,{"derivedFrom":sQuery(id+"F4.wireOp",EDGE,"E40.1.0")}),1.0]])]});
            var Q12;
            Q12=makeQuery(id+"F4.imprint","IMPRINT",FACE,{"disambiguationData":[TD([[makeQuery(id+"F4.imprint","IMPRINT",EDGE,{"derivedFrom":sQuery(id+"F4.wireOp",EDGE,"E18")}),-1.0]])]});
            var Q13;
            Q13=makeQuery(id+"F4.imprint","IMPRINT",FACE,{"disambiguationData":[TD([[makeQuery(id+"F4.imprint","IMPRINT",EDGE,{"derivedFrom":sQuery(id+"F4.wireOp",EDGE,"E21")}),-1.0]])]});
            var Q14;
            Q14=makeQuery(id+"F4.imprint","IMPRINT",FACE,{"disambiguationData":[TD([[makeQuery(id+"F4.imprint","IMPRINT",EDGE,{"derivedFrom":sQuery(id+"F4.wireOp",EDGE,"E16")}),-1.0]])]});
            var Q15;
            Q15=makeQuery(id+"F4.imprint","IMPRINT",FACE,{"disambiguationData":[TD([[makeQuery(id+"F4.imprint","IMPRINT",EDGE,{"derivedFrom":sQuery(id+"F4.wireOp",EDGE,"E25")}),-1.0]])]});
            extrude(context, id + "F5", {"entities" : qUnion([Q0, Q1, Q2, Q3, Q4, Q5, Q6, Q7, Q8, Q9, Q10, Q11, Q12, Q13, Q14, Q15]), "operationType" : NewBodyOperationType.REMOVE, "oppositeDirection" : true, "depth" : 4.5 * mm});
        }
        {
            var Q0;
            Q0=makeQuery(id+"F4.imprint","IMPRINT",FACE,{"disambiguationData":[TD([[makeQuery(id+"F4.imprint","IMPRINT",EDGE,{"derivedFrom":sQuery(id+"F4.wireOp",EDGE,"E40.3.6")}),-1.0]])]});
            var Q1;
            Q1=makeQuery(id+"F4.imprint","IMPRINT",FACE,{"disambiguationData":[TD([[makeQuery(id+"F4.imprint","IMPRINT",EDGE,{"derivedFrom":sQuery(id+"F4.wireOp",EDGE,"E40.3.2")}),-1.0]])]});
            var Q2;
            Q2=makeQuery(id+"F4.imprint","IMPRINT",FACE,{"disambiguationData":[TD([[makeQuery(id+"F4.imprint","IMPRINT",EDGE,{"derivedFrom":sQuery(id+"F4.wireOp",EDGE,"E40.2.6")}),-1.0]])]});
            var Q3;
            Q3=makeQuery(id+"F4.imprint","IMPRINT",FACE,{"disambiguationData":[TD([[makeQuery(id+"F4.imprint","IMPRINT",EDGE,{"derivedFrom":sQuery(id+"F4.wireOp",EDGE,"E40.2.2")}),-1.0]])]});
            var Q4;
            Q4=makeQuery(id+"F4.imprint","IMPRINT",FACE,{"disambiguationData":[TD([[makeQuery(id+"F4.imprint","IMPRINT",EDGE,{"derivedFrom":sQuery(id+"F4.wireOp",EDGE,"E40.1.6")}),-1.0]])]});
            var Q5;
            Q5=makeQuery(id+"F4.imprint","IMPRINT",FACE,{"disambiguationData":[TD([[makeQuery(id+"F4.imprint","IMPRINT",EDGE,{"derivedFrom":sQuery(id+"F4.wireOp",EDGE,"E40.1.2")}),-1.0]])]});
            var Q6;
            Q6=makeQuery(id+"F4.imprint","IMPRINT",FACE,{"disambiguationData":[TD([[makeQuery(id+"F4.imprint","IMPRINT",EDGE,{"derivedFrom":sQuery(id+"F4.wireOp",EDGE,"E23")}),-1.0]])]});
            var Q7;
            Q7=makeQuery(id+"F4.imprint","IMPRINT",FACE,{"disambiguationData":[TD([[makeQuery(id+"F4.imprint","IMPRINT",EDGE,{"derivedFrom":sQuery(id+"F4.wireOp",EDGE,"E27")}),-1.0]])]});
            extrude(context, id + "F6", {"entities" : qUnion([Q0, Q1, Q2, Q3, Q4, Q5, Q6, Q7]), "operationType" : NewBodyOperationType.REMOVE, "oppositeDirection" : true, "depth" : 2.5 * mm});
        }
        {
            var Q0;
            Q0=makeQuery(id+"F5.boolean.opBoolean","COPY",EDGE,{"derivedFrom":makeQuery(id+"F5.opExtrude","SWEPT_EDGE",EDGE,{"disambiguationData":[OSD([sQuery(id+"F4.wireOp",EDGE,"E40.3.8"),sQuery(id+"F4.wireOp",EDGE,"E40.3.11")])]})});
            var Q1;
            Q1=makeQuery(id+"F5.boolean.opBoolean","COPY",EDGE,{"derivedFrom":makeQuery(id+"F5.opExtrude","SWEPT_EDGE",EDGE,{"disambiguationData":[OSD([sQuery(id+"F4.wireOp",EDGE,"E40.3.10"),sQuery(id+"F4.wireOp",EDGE,"E40.3.19")])]})});
            var Q2;
            Q2=makeQuery(id+"F6.boolean.opBoolean","COPY",EDGE,{"derivedFrom":makeQuery(id+"F6.opExtrude","SWEPT_EDGE",EDGE,{"disambiguationData":[OSD([sQuery(id+"F4.wireOp",EDGE,"E40.3.6"),sQuery(id+"F4.wireOp",EDGE,"E40.3.20")])]})});
            var Q3;
            Q3=makeQuery(id+"F5.boolean.opBoolean","COPY",EDGE,{"derivedFrom":makeQuery(id+"F5.opExtrude","SWEPT_EDGE",EDGE,{"disambiguationData":[OSD([sQuery(id+"F4.wireOp",EDGE,"E40.3.14"),sQuery(id+"F4.wireOp",EDGE,"E40.3.15")])]})});
            var Q4;
            Q4=makeQuery(id+"F6.boolean.opBoolean","COPY",EDGE,{"derivedFrom":makeQuery(id+"F6.opExtrude","SWEPT_EDGE",EDGE,{"disambiguationData":[OSD([sQuery(id+"F4.wireOp",EDGE,"E40.3.2"),sQuery(id+"F4.wireOp",EDGE,"E40.3.17")])]})});
            var Q5;
            Q5=makeQuery(id+"F5.boolean.opBoolean","COPY",EDGE,{"derivedFrom":makeQuery(id+"F5.opExtrude","SWEPT_EDGE",EDGE,{"disambiguationData":[OSD([sQuery(id+"F4.wireOp",EDGE,"E40.3.1"),sQuery(id+"F4.wireOp",EDGE,"E40.3.12")])]})});
            var Q6;
            Q6=makeQuery(id+"F5.boolean.opBoolean","COPY",EDGE,{"derivedFrom":makeQuery(id+"F5.opExtrude","SWEPT_EDGE",EDGE,{"disambiguationData":[OSD([sQuery(id+"F4.wireOp",EDGE,"E40.3.4"),sQuery(id+"F4.wireOp",EDGE,"E40.3.8")])]})});
            var Q7;
            Q7=makeQuery(id+"F5.boolean.opBoolean","COPY",EDGE,{"derivedFrom":makeQuery(id+"F5.opExtrude","SWEPT_EDGE",EDGE,{"disambiguationData":[OSD([sQuery(id+"F4.wireOp",EDGE,"E40.3.3"),sQuery(id+"F4.wireOp",EDGE,"E40.3.10")])]})});
            var Q8;
            Q8=makeQuery(id+"F6.boolean.opBoolean","COPY",EDGE,{"derivedFrom":makeQuery(id+"F6.opExtrude","SWEPT_EDGE",EDGE,{"disambiguationData":[OSD([sQuery(id+"F4.wireOp",EDGE,"E40.3.6"),sQuery(id+"F4.wireOp",EDGE,"E40.3.21")])]})});
            var Q9;
            Q9=makeQuery(id+"F5.boolean.opBoolean","COPY",EDGE,{"derivedFrom":makeQuery(id+"F5.opExtrude","SWEPT_EDGE",EDGE,{"disambiguationData":[OSD([sQuery(id+"F4.wireOp",EDGE,"E40.3.14"),sQuery(id+"F4.wireOp",EDGE,"E40.3.23")])]})});
            var Q10;
            Q10=makeQuery(id+"F6.boolean.opBoolean","COPY",EDGE,{"derivedFrom":makeQuery(id+"F6.opExtrude","SWEPT_EDGE",EDGE,{"disambiguationData":[OSD([sQuery(id+"F4.wireOp",EDGE,"E40.3.2"),sQuery(id+"F4.wireOp",EDGE,"E40.3.22")])]})});
            var Q11;
            Q11=makeQuery(id+"F5.boolean.opBoolean","COPY",EDGE,{"derivedFrom":makeQuery(id+"F5.opExtrude","SWEPT_EDGE",EDGE,{"disambiguationData":[OSD([sQuery(id+"F4.wireOp",EDGE,"E40.3.7"),sQuery(id+"F4.wireOp",EDGE,"E40.3.12")])]})});
            var Q12;
            Q12=makeQuery(id+"F5.boolean.opBoolean","COPY",EDGE,{"derivedFrom":makeQuery(id+"F5.opExtrude","SWEPT_EDGE",EDGE,{"disambiguationData":[OSD([sQuery(id+"F4.wireOp",EDGE,"E40.2.4"),sQuery(id+"F4.wireOp",EDGE,"E40.2.5")])]})});
            var Q13;
            Q13=makeQuery(id+"F5.boolean.opBoolean","COPY",EDGE,{"derivedFrom":makeQuery(id+"F5.opExtrude","SWEPT_EDGE",EDGE,{"disambiguationData":[OSD([sQuery(id+"F4.wireOp",EDGE,"E40.2.3"),sQuery(id+"F4.wireOp",EDGE,"E40.2.9")])]})});
            var Q14;
            Q14=makeQuery(id+"F6.boolean.opBoolean","COPY",EDGE,{"derivedFrom":makeQuery(id+"F6.opExtrude","SWEPT_EDGE",EDGE,{"disambiguationData":[OSD([sQuery(id+"F4.wireOp",EDGE,"E40.2.13"),sQuery(id+"F4.wireOp",EDGE,"E40.2.21")])]})});
            var Q15;
            Q15=makeQuery(id+"F5.boolean.opBoolean","COPY",EDGE,{"derivedFrom":makeQuery(id+"F5.opExtrude","SWEPT_EDGE",EDGE,{"disambiguationData":[OSD([sQuery(id+"F4.wireOp",EDGE,"E40.2.16"),sQuery(id+"F4.wireOp",EDGE,"E40.2.23")])]})});
            var Q16;
            Q16=makeQuery(id+"F6.boolean.opBoolean","COPY",EDGE,{"derivedFrom":makeQuery(id+"F6.opExtrude","SWEPT_EDGE",EDGE,{"disambiguationData":[OSD([sQuery(id+"F4.wireOp",EDGE,"E40.2.18"),sQuery(id+"F4.wireOp",EDGE,"E40.2.22")])]})});
            var Q17;
            Q17=makeQuery(id+"F5.boolean.opBoolean","COPY",EDGE,{"derivedFrom":makeQuery(id+"F5.opExtrude","SWEPT_EDGE",EDGE,{"disambiguationData":[OSD([sQuery(id+"F4.wireOp",EDGE,"E40.2.0"),sQuery(id+"F4.wireOp",EDGE,"E40.2.7")])]})});
            var Q18;
            Q18=makeQuery(id+"F5.boolean.opBoolean","COPY",EDGE,{"derivedFrom":makeQuery(id+"F5.opExtrude","SWEPT_EDGE",EDGE,{"disambiguationData":[OSD([sQuery(id+"F4.wireOp",EDGE,"E40.3.4"),sQuery(id+"F4.wireOp",EDGE,"E40.3.5")])]})});
            var Q19;
            Q19=makeQuery(id+"F5.boolean.opBoolean","COPY",EDGE,{"derivedFrom":makeQuery(id+"F5.opExtrude","SWEPT_EDGE",EDGE,{"disambiguationData":[OSD([sQuery(id+"F4.wireOp",EDGE,"E40.3.3"),sQuery(id+"F4.wireOp",EDGE,"E40.3.9")])]})});
            var Q20;
            Q20=makeQuery(id+"F6.boolean.opBoolean","COPY",EDGE,{"derivedFrom":makeQuery(id+"F6.opExtrude","SWEPT_EDGE",EDGE,{"disambiguationData":[OSD([sQuery(id+"F4.wireOp",EDGE,"E40.3.13"),sQuery(id+"F4.wireOp",EDGE,"E40.3.21")])]})});
            var Q21;
            Q21=makeQuery(id+"F5.boolean.opBoolean","COPY",EDGE,{"derivedFrom":makeQuery(id+"F5.opExtrude","SWEPT_EDGE",EDGE,{"disambiguationData":[OSD([sQuery(id+"F4.wireOp",EDGE,"E40.3.16"),sQuery(id+"F4.wireOp",EDGE,"E40.3.23")])]})});
            var Q22;
            Q22=makeQuery(id+"F6.boolean.opBoolean","COPY",EDGE,{"derivedFrom":makeQuery(id+"F6.opExtrude","SWEPT_EDGE",EDGE,{"disambiguationData":[OSD([sQuery(id+"F4.wireOp",EDGE,"E40.3.18"),sQuery(id+"F4.wireOp",EDGE,"E40.3.22")])]})});
            var Q23;
            Q23=makeQuery(id+"F5.boolean.opBoolean","COPY",EDGE,{"derivedFrom":makeQuery(id+"F5.opExtrude","SWEPT_EDGE",EDGE,{"disambiguationData":[OSD([sQuery(id+"F4.wireOp",EDGE,"E40.3.0"),sQuery(id+"F4.wireOp",EDGE,"E40.3.7")])]})});
            var Q24;
            Q24=makeQuery(id+"F5.boolean.opBoolean","COPY",EDGE,{"derivedFrom":makeQuery(id+"F5.opExtrude","SWEPT_EDGE",EDGE,{"disambiguationData":[OSD([sQuery(id+"F4.wireOp",EDGE,"E40.3.5"),sQuery(id+"F4.wireOp",EDGE,"E40.3.11")])]})});
            var Q25;
            Q25=makeQuery(id+"F5.boolean.opBoolean","COPY",EDGE,{"derivedFrom":makeQuery(id+"F5.opExtrude","SWEPT_EDGE",EDGE,{"disambiguationData":[OSD([sQuery(id+"F4.wireOp",EDGE,"E40.3.9"),sQuery(id+"F4.wireOp",EDGE,"E40.3.19")])]})});
            var Q26;
            Q26=makeQuery(id+"F6.boolean.opBoolean","COPY",EDGE,{"derivedFrom":makeQuery(id+"F6.opExtrude","SWEPT_EDGE",EDGE,{"disambiguationData":[OSD([sQuery(id+"F4.wireOp",EDGE,"E40.3.13"),sQuery(id+"F4.wireOp",EDGE,"E40.3.20")])]})});
            var Q27;
            Q27=makeQuery(id+"F5.boolean.opBoolean","COPY",EDGE,{"derivedFrom":makeQuery(id+"F5.opExtrude","SWEPT_EDGE",EDGE,{"disambiguationData":[OSD([sQuery(id+"F4.wireOp",EDGE,"E40.3.15"),sQuery(id+"F4.wireOp",EDGE,"E40.3.16")])]})});
            var Q28;
            Q28=makeQuery(id+"F6.boolean.opBoolean","COPY",EDGE,{"derivedFrom":makeQuery(id+"F6.opExtrude","SWEPT_EDGE",EDGE,{"disambiguationData":[OSD([sQuery(id+"F4.wireOp",EDGE,"E40.3.17"),sQuery(id+"F4.wireOp",EDGE,"E40.3.18")])]})});
            var Q29;
            Q29=makeQuery(id+"F5.boolean.opBoolean","COPY",EDGE,{"derivedFrom":makeQuery(id+"F5.opExtrude","SWEPT_EDGE",EDGE,{"disambiguationData":[OSD([sQuery(id+"F4.wireOp",EDGE,"E40.3.0"),sQuery(id+"F4.wireOp",EDGE,"E40.3.1")])]})});
            var Q30;
            Q30=makeQuery(id+"F5.boolean.opBoolean","COPY",EDGE,{"derivedFrom":makeQuery(id+"F5.opExtrude","SWEPT_EDGE",EDGE,{"disambiguationData":[OSD([sQuery(id+"F4.wireOp",EDGE,"E40.2.5"),sQuery(id+"F4.wireOp",EDGE,"E40.2.11")])]})});
            var Q31;
            Q31=makeQuery(id+"F5.boolean.opBoolean","COPY",EDGE,{"derivedFrom":makeQuery(id+"F5.opExtrude","SWEPT_EDGE",EDGE,{"disambiguationData":[OSD([sQuery(id+"F4.wireOp",EDGE,"E40.2.9"),sQuery(id+"F4.wireOp",EDGE,"E40.2.19")])]})});
            var Q32;
            Q32=makeQuery(id+"F6.boolean.opBoolean","COPY",EDGE,{"derivedFrom":makeQuery(id+"F6.opExtrude","SWEPT_EDGE",EDGE,{"disambiguationData":[OSD([sQuery(id+"F4.wireOp",EDGE,"E40.2.13"),sQuery(id+"F4.wireOp",EDGE,"E40.2.20")])]})});
            var Q33;
            Q33=makeQuery(id+"F5.boolean.opBoolean","COPY",EDGE,{"derivedFrom":makeQuery(id+"F5.opExtrude","SWEPT_EDGE",EDGE,{"disambiguationData":[OSD([sQuery(id+"F4.wireOp",EDGE,"E40.2.15"),sQuery(id+"F4.wireOp",EDGE,"E40.2.16")])]})});
            var Q34;
            Q34=makeQuery(id+"F6.boolean.opBoolean","COPY",EDGE,{"derivedFrom":makeQuery(id+"F6.opExtrude","SWEPT_EDGE",EDGE,{"disambiguationData":[OSD([sQuery(id+"F4.wireOp",EDGE,"E40.2.17"),sQuery(id+"F4.wireOp",EDGE,"E40.2.18")])]})});
            var Q35;
            Q35=makeQuery(id+"F5.boolean.opBoolean","COPY",EDGE,{"derivedFrom":makeQuery(id+"F5.opExtrude","SWEPT_EDGE",EDGE,{"disambiguationData":[OSD([sQuery(id+"F4.wireOp",EDGE,"E40.2.0"),sQuery(id+"F4.wireOp",EDGE,"E40.2.1")])]})});
            var Q36;
            Q36=makeQuery(id+"F5.boolean.opBoolean","COPY",EDGE,{"derivedFrom":makeQuery(id+"F5.opExtrude","SWEPT_EDGE",EDGE,{"disambiguationData":[OSD([sQuery(id+"F4.wireOp",EDGE,"E40.2.1"),sQuery(id+"F4.wireOp",EDGE,"E40.2.12")])]})});
            var Q37;
            Q37=makeQuery(id+"F6.boolean.opBoolean","COPY",EDGE,{"derivedFrom":makeQuery(id+"F6.opExtrude","SWEPT_EDGE",EDGE,{"disambiguationData":[OSD([sQuery(id+"F4.wireOp",EDGE,"E40.2.2"),sQuery(id+"F4.wireOp",EDGE,"E40.2.17")])]})});
            var Q38;
            Q38=makeQuery(id+"F5.boolean.opBoolean","COPY",EDGE,{"derivedFrom":makeQuery(id+"F5.opExtrude","SWEPT_EDGE",EDGE,{"disambiguationData":[OSD([sQuery(id+"F4.wireOp",EDGE,"E40.2.14"),sQuery(id+"F4.wireOp",EDGE,"E40.2.15")])]})});
            var Q39;
            Q39=makeQuery(id+"F5.boolean.opBoolean","COPY",EDGE,{"derivedFrom":makeQuery(id+"F5.opExtrude","SWEPT_EDGE",EDGE,{"disambiguationData":[OSD([sQuery(id+"F4.wireOp",EDGE,"E40.2.8"),sQuery(id+"F4.wireOp",EDGE,"E40.2.11")])]})});
            var Q40;
            Q40=makeQuery(id+"F5.boolean.opBoolean","COPY",EDGE,{"derivedFrom":makeQuery(id+"F5.opExtrude","SWEPT_EDGE",EDGE,{"disambiguationData":[OSD([sQuery(id+"F4.wireOp",EDGE,"E40.2.10"),sQuery(id+"F4.wireOp",EDGE,"E40.2.19")])]})});
            var Q41;
            Q41=makeQuery(id+"F6.boolean.opBoolean","COPY",EDGE,{"derivedFrom":makeQuery(id+"F6.opExtrude","SWEPT_EDGE",EDGE,{"disambiguationData":[OSD([sQuery(id+"F4.wireOp",EDGE,"E40.2.6"),sQuery(id+"F4.wireOp",EDGE,"E40.2.20")])]})});
            var Q42;
            Q42=makeQuery(id+"F5.boolean.opBoolean","COPY",EDGE,{"derivedFrom":makeQuery(id+"F5.opExtrude","SWEPT_EDGE",EDGE,{"disambiguationData":[OSD([sQuery(id+"F4.wireOp",EDGE,"E40.2.4"),sQuery(id+"F4.wireOp",EDGE,"E40.2.8")])]})});
            var Q43;
            Q43=makeQuery(id+"F5.boolean.opBoolean","COPY",EDGE,{"derivedFrom":makeQuery(id+"F5.opExtrude","SWEPT_EDGE",EDGE,{"disambiguationData":[OSD([sQuery(id+"F4.wireOp",EDGE,"E40.2.3"),sQuery(id+"F4.wireOp",EDGE,"E40.2.10")])]})});
            var Q44;
            Q44=makeQuery(id+"F6.boolean.opBoolean","COPY",EDGE,{"derivedFrom":makeQuery(id+"F6.opExtrude","SWEPT_EDGE",EDGE,{"disambiguationData":[OSD([sQuery(id+"F4.wireOp",EDGE,"E40.2.6"),sQuery(id+"F4.wireOp",EDGE,"E40.2.21")])]})});
            var Q45;
            Q45=makeQuery(id+"F5.boolean.opBoolean","COPY",EDGE,{"derivedFrom":makeQuery(id+"F5.opExtrude","SWEPT_EDGE",EDGE,{"disambiguationData":[OSD([sQuery(id+"F4.wireOp",EDGE,"E40.2.14"),sQuery(id+"F4.wireOp",EDGE,"E40.2.23")])]})});
            var Q46;
            Q46=makeQuery(id+"F5.boolean.opBoolean","COPY",EDGE,{"derivedFrom":makeQuery(id+"F5.opExtrude","SWEPT_EDGE",EDGE,{"disambiguationData":[OSD([sQuery(id+"F4.wireOp",EDGE,"E40.2.7"),sQuery(id+"F4.wireOp",EDGE,"E40.2.12")])]})});
            var Q47;
            Q47=makeQuery(id+"F6.boolean.opBoolean","COPY",EDGE,{"derivedFrom":makeQuery(id+"F6.opExtrude","SWEPT_EDGE",EDGE,{"disambiguationData":[OSD([sQuery(id+"F4.wireOp",EDGE,"E40.2.2"),sQuery(id+"F4.wireOp",EDGE,"E40.2.22")])]})});
            var Q48;
            Q48=makeQuery(id+"F5.boolean.opBoolean","COPY",EDGE,{"derivedFrom":makeQuery(id+"F5.opExtrude","SWEPT_EDGE",EDGE,{"disambiguationData":[OSD([sQuery(id+"F4.wireOp",EDGE,"E40.1.4"),sQuery(id+"F4.wireOp",EDGE,"E40.1.5")])]})});
            var Q49;
            Q49=makeQuery(id+"F5.boolean.opBoolean","COPY",EDGE,{"derivedFrom":makeQuery(id+"F5.opExtrude","SWEPT_EDGE",EDGE,{"disambiguationData":[OSD([sQuery(id+"F4.wireOp",EDGE,"E40.1.3"),sQuery(id+"F4.wireOp",EDGE,"E40.1.9")])]})});
            var Q50;
            Q50=makeQuery(id+"F6.boolean.opBoolean","COPY",EDGE,{"derivedFrom":makeQuery(id+"F6.opExtrude","SWEPT_EDGE",EDGE,{"disambiguationData":[OSD([sQuery(id+"F4.wireOp",EDGE,"E40.1.13"),sQuery(id+"F4.wireOp",EDGE,"E40.1.21")])]})});
            var Q51;
            Q51=makeQuery(id+"F5.boolean.opBoolean","COPY",EDGE,{"derivedFrom":makeQuery(id+"F5.opExtrude","SWEPT_EDGE",EDGE,{"disambiguationData":[OSD([sQuery(id+"F4.wireOp",EDGE,"E40.1.16"),sQuery(id+"F4.wireOp",EDGE,"E40.1.23")])]})});
            var Q52;
            Q52=makeQuery(id+"F6.boolean.opBoolean","COPY",EDGE,{"derivedFrom":makeQuery(id+"F6.opExtrude","SWEPT_EDGE",EDGE,{"disambiguationData":[OSD([sQuery(id+"F4.wireOp",EDGE,"E40.1.18"),sQuery(id+"F4.wireOp",EDGE,"E40.1.22")])]})});
            var Q53;
            Q53=makeQuery(id+"F5.boolean.opBoolean","COPY",EDGE,{"derivedFrom":makeQuery(id+"F5.opExtrude","SWEPT_EDGE",EDGE,{"disambiguationData":[OSD([sQuery(id+"F4.wireOp",EDGE,"E40.1.0"),sQuery(id+"F4.wireOp",EDGE,"E40.1.7")])]})});
            var Q54;
            Q54=makeQuery(id+"F5.boolean.opBoolean","COPY",EDGE,{"derivedFrom":makeQuery(id+"F5.opExtrude","SWEPT_EDGE",EDGE,{"disambiguationData":[OSD([sQuery(id+"F4.wireOp",EDGE,"E40.1.4"),sQuery(id+"F4.wireOp",EDGE,"E40.1.8")])]})});
            var Q55;
            Q55=makeQuery(id+"F5.boolean.opBoolean","COPY",EDGE,{"derivedFrom":makeQuery(id+"F5.opExtrude","SWEPT_EDGE",EDGE,{"disambiguationData":[OSD([sQuery(id+"F4.wireOp",EDGE,"E40.1.3"),sQuery(id+"F4.wireOp",EDGE,"E40.1.10")])]})});
            var Q56;
            Q56=makeQuery(id+"F6.boolean.opBoolean","COPY",EDGE,{"derivedFrom":makeQuery(id+"F6.opExtrude","SWEPT_EDGE",EDGE,{"disambiguationData":[OSD([sQuery(id+"F4.wireOp",EDGE,"E40.1.6"),sQuery(id+"F4.wireOp",EDGE,"E40.1.21")])]})});
            var Q57;
            Q57=makeQuery(id+"F5.boolean.opBoolean","COPY",EDGE,{"derivedFrom":makeQuery(id+"F5.opExtrude","SWEPT_EDGE",EDGE,{"disambiguationData":[OSD([sQuery(id+"F4.wireOp",EDGE,"E40.1.14"),sQuery(id+"F4.wireOp",EDGE,"E40.1.23")])]})});
            var Q58;
            Q58=makeQuery(id+"F5.boolean.opBoolean","COPY",EDGE,{"derivedFrom":makeQuery(id+"F5.opExtrude","SWEPT_EDGE",EDGE,{"disambiguationData":[OSD([sQuery(id+"F4.wireOp",EDGE,"E40.1.7"),sQuery(id+"F4.wireOp",EDGE,"E40.1.12")])]})});
            var Q59;
            Q59=makeQuery(id+"F6.boolean.opBoolean","COPY",EDGE,{"derivedFrom":makeQuery(id+"F6.opExtrude","SWEPT_EDGE",EDGE,{"disambiguationData":[OSD([sQuery(id+"F4.wireOp",EDGE,"E40.1.2"),sQuery(id+"F4.wireOp",EDGE,"E40.1.22")])]})});
            var Q60;
            Q60=makeQuery(id+"F5.boolean.opBoolean","COPY",EDGE,{"derivedFrom":makeQuery(id+"F5.opExtrude","SWEPT_EDGE",EDGE,{"disambiguationData":[OSD([sQuery(id+"F4.wireOp",EDGE,"E40.1.5"),sQuery(id+"F4.wireOp",EDGE,"E40.1.11")])]})});
            var Q61;
            Q61=makeQuery(id+"F5.boolean.opBoolean","COPY",EDGE,{"derivedFrom":makeQuery(id+"F5.opExtrude","SWEPT_EDGE",EDGE,{"disambiguationData":[OSD([sQuery(id+"F4.wireOp",EDGE,"E40.1.9"),sQuery(id+"F4.wireOp",EDGE,"E40.1.19")])]})});
            var Q62;
            Q62=makeQuery(id+"F6.boolean.opBoolean","COPY",EDGE,{"derivedFrom":makeQuery(id+"F6.opExtrude","SWEPT_EDGE",EDGE,{"disambiguationData":[OSD([sQuery(id+"F4.wireOp",EDGE,"E40.1.13"),sQuery(id+"F4.wireOp",EDGE,"E40.1.20")])]})});
            var Q63;
            Q63=makeQuery(id+"F5.boolean.opBoolean","COPY",EDGE,{"derivedFrom":makeQuery(id+"F5.opExtrude","SWEPT_EDGE",EDGE,{"disambiguationData":[OSD([sQuery(id+"F4.wireOp",EDGE,"E40.1.15"),sQuery(id+"F4.wireOp",EDGE,"E40.1.16")])]})});
            var Q64;
            Q64=makeQuery(id+"F6.boolean.opBoolean","COPY",EDGE,{"derivedFrom":makeQuery(id+"F6.opExtrude","SWEPT_EDGE",EDGE,{"disambiguationData":[OSD([sQuery(id+"F4.wireOp",EDGE,"E40.1.17"),sQuery(id+"F4.wireOp",EDGE,"E40.1.18")])]})});
            var Q65;
            Q65=makeQuery(id+"F5.boolean.opBoolean","COPY",EDGE,{"derivedFrom":makeQuery(id+"F5.opExtrude","SWEPT_EDGE",EDGE,{"disambiguationData":[OSD([sQuery(id+"F4.wireOp",EDGE,"E40.1.0"),sQuery(id+"F4.wireOp",EDGE,"E40.1.1")])]})});
            var Q66;
            Q66=makeQuery(id+"F5.boolean.opBoolean","COPY",EDGE,{"derivedFrom":makeQuery(id+"F5.opExtrude","SWEPT_EDGE",EDGE,{"disambiguationData":[OSD([sQuery(id+"F4.wireOp",EDGE,"E40.1.8"),sQuery(id+"F4.wireOp",EDGE,"E40.1.11")])]})});
            var Q67;
            Q67=makeQuery(id+"F5.boolean.opBoolean","COPY",EDGE,{"derivedFrom":makeQuery(id+"F5.opExtrude","SWEPT_EDGE",EDGE,{"disambiguationData":[OSD([sQuery(id+"F4.wireOp",EDGE,"E40.1.10"),sQuery(id+"F4.wireOp",EDGE,"E40.1.19")])]})});
            var Q68;
            Q68=makeQuery(id+"F6.boolean.opBoolean","COPY",EDGE,{"derivedFrom":makeQuery(id+"F6.opExtrude","SWEPT_EDGE",EDGE,{"disambiguationData":[OSD([sQuery(id+"F4.wireOp",EDGE,"E40.1.6"),sQuery(id+"F4.wireOp",EDGE,"E40.1.20")])]})});
            var Q69;
            Q69=makeQuery(id+"F5.boolean.opBoolean","COPY",EDGE,{"derivedFrom":makeQuery(id+"F5.opExtrude","SWEPT_EDGE",EDGE,{"disambiguationData":[OSD([sQuery(id+"F4.wireOp",EDGE,"E40.1.14"),sQuery(id+"F4.wireOp",EDGE,"E40.1.15")])]})});
            var Q70;
            Q70=makeQuery(id+"F6.boolean.opBoolean","COPY",EDGE,{"derivedFrom":makeQuery(id+"F6.opExtrude","SWEPT_EDGE",EDGE,{"disambiguationData":[OSD([sQuery(id+"F4.wireOp",EDGE,"E40.1.2"),sQuery(id+"F4.wireOp",EDGE,"E40.1.17")])]})});
            var Q71;
            Q71=makeQuery(id+"F5.boolean.opBoolean","COPY",EDGE,{"derivedFrom":makeQuery(id+"F5.opExtrude","SWEPT_EDGE",EDGE,{"disambiguationData":[OSD([sQuery(id+"F4.wireOp",EDGE,"E40.1.1"),sQuery(id+"F4.wireOp",EDGE,"E40.1.12")])]})});
            var Q72;
            Q72=makeQuery(id+"F5.boolean.opBoolean","COPY",EDGE,{"derivedFrom":makeQuery(id+"F5.opExtrude","SWEPT_EDGE",EDGE,{"disambiguationData":[OSD([sQuery(id+"F4.wireOp",EDGE,"E18"),sQuery(id+"F4.wireOp",EDGE,"E30.trimOffspring")])]})});
            var Q73;
            Q73=makeQuery(id+"F5.boolean.opBoolean","COPY",EDGE,{"derivedFrom":makeQuery(id+"F5.opExtrude","SWEPT_EDGE",EDGE,{"disambiguationData":[OSD([sQuery(id+"F4.wireOp",EDGE,"E21"),sQuery(id+"F4.wireOp",EDGE,"E33.trimOffspring")])]})});
            var Q74;
            Q74=makeQuery(id+"F6.boolean.opBoolean","COPY",EDGE,{"derivedFrom":makeQuery(id+"F6.opExtrude","SWEPT_EDGE",EDGE,{"disambiguationData":[OSD([sQuery(id+"F4.wireOp",EDGE,"E23"),sQuery(id+"F4.wireOp",EDGE,"E34.trimOffspring")])]})});
            var Q75;
            Q75=makeQuery(id+"F5.boolean.opBoolean","COPY",EDGE,{"derivedFrom":makeQuery(id+"F5.opExtrude","SWEPT_EDGE",EDGE,{"disambiguationData":[OSD([sQuery(id+"F4.wireOp",EDGE,"E25"),sQuery(id+"F4.wireOp",EDGE,"E36.trimOffspring")])]})});
            var Q76;
            Q76=makeQuery(id+"F6.boolean.opBoolean","COPY",EDGE,{"derivedFrom":makeQuery(id+"F6.opExtrude","SWEPT_EDGE",EDGE,{"disambiguationData":[OSD([sQuery(id+"F4.wireOp",EDGE,"E27"),sQuery(id+"F4.wireOp",EDGE,"E35.trimOffspring")])]})});
            var Q77;
            Q77=makeQuery(id+"F5.boolean.opBoolean","COPY",EDGE,{"derivedFrom":makeQuery(id+"F5.opExtrude","SWEPT_EDGE",EDGE,{"disambiguationData":[OSD([sQuery(id+"F4.wireOp",EDGE,"E17"),sQuery(id+"F4.wireOp",EDGE,"E29")])]})});
            var Q78;
            Q78=makeQuery(id+"F5.boolean.opBoolean","COPY",EDGE,{"derivedFrom":makeQuery(id+"F5.opExtrude","SWEPT_EDGE",EDGE,{"disambiguationData":[OSD([sQuery(id+"F4.wireOp",EDGE,"E20"),sQuery(id+"F4.wireOp",EDGE,"E30.trimOffspring")])]})});
            var Q79;
            Q79=makeQuery(id+"F5.boolean.opBoolean","COPY",EDGE,{"derivedFrom":makeQuery(id+"F5.opExtrude","SWEPT_EDGE",EDGE,{"disambiguationData":[OSD([sQuery(id+"F4.wireOp",EDGE,"E22"),sQuery(id+"F4.wireOp",EDGE,"E33.trimOffspring")])]})});
            var Q80;
            Q80=makeQuery(id+"F6.boolean.opBoolean","COPY",EDGE,{"derivedFrom":makeQuery(id+"F6.opExtrude","SWEPT_EDGE",EDGE,{"disambiguationData":[OSD([sQuery(id+"F4.wireOp",EDGE,"E24"),sQuery(id+"F4.wireOp",EDGE,"E34.trimOffspring")])]})});
            var Q81;
            Q81=makeQuery(id+"F5.boolean.opBoolean","COPY",EDGE,{"derivedFrom":makeQuery(id+"F5.opExtrude","SWEPT_EDGE",EDGE,{"disambiguationData":[OSD([sQuery(id+"F4.wireOp",EDGE,"E26"),sQuery(id+"F4.wireOp",EDGE,"E36.trimOffspring")])]})});
            var Q82;
            Q82=makeQuery(id+"F6.boolean.opBoolean","COPY",EDGE,{"derivedFrom":makeQuery(id+"F6.opExtrude","SWEPT_EDGE",EDGE,{"disambiguationData":[OSD([sQuery(id+"F4.wireOp",EDGE,"E28"),sQuery(id+"F4.wireOp",EDGE,"E35.trimOffspring")])]})});
            var Q83;
            Q83=makeQuery(id+"F5.boolean.opBoolean","COPY",EDGE,{"derivedFrom":makeQuery(id+"F5.opExtrude","SWEPT_EDGE",EDGE,{"disambiguationData":[OSD([sQuery(id+"F4.wireOp",EDGE,"E17"),sQuery(id+"F4.wireOp",EDGE,"E19")])]})});
            var Q84;
            Q84=makeQuery(id+"F5.boolean.opBoolean","COPY",EDGE,{"derivedFrom":makeQuery(id+"F5.opExtrude","SWEPT_EDGE",EDGE,{"disambiguationData":[OSD([sQuery(id+"F4.wireOp",EDGE,"E20"),sQuery(id+"F4.wireOp",EDGE,"E31.trimOffspring")])]})});
            var Q85;
            Q85=makeQuery(id+"F5.boolean.opBoolean","COPY",EDGE,{"derivedFrom":makeQuery(id+"F5.opExtrude","SWEPT_EDGE",EDGE,{"disambiguationData":[OSD([sQuery(id+"F4.wireOp",EDGE,"E18"),sQuery(id+"F4.wireOp",EDGE,"E31.trimOffspring")])]})});
            var Q86;
            Q86=makeQuery(id+"F5.boolean.opBoolean","COPY",EDGE,{"derivedFrom":makeQuery(id+"F5.opExtrude","SWEPT_EDGE",EDGE,{"disambiguationData":[OSD([sQuery(id+"F4.wireOp",EDGE,"E21"),sQuery(id+"F4.wireOp",EDGE,"E32.trimOffspring")])]})});
            var Q87;
            Q87=makeQuery(id+"F5.boolean.opBoolean","COPY",EDGE,{"derivedFrom":makeQuery(id+"F5.opExtrude","SWEPT_EDGE",EDGE,{"disambiguationData":[OSD([sQuery(id+"F4.wireOp",EDGE,"E22"),sQuery(id+"F4.wireOp",EDGE,"E32.trimOffspring")])]})});
            var Q88;
            Q88=makeQuery(id+"F6.boolean.opBoolean","COPY",EDGE,{"derivedFrom":makeQuery(id+"F6.opExtrude","SWEPT_EDGE",EDGE,{"disambiguationData":[OSD([sQuery(id+"F4.wireOp",EDGE,"E23"),sQuery(id+"F4.wireOp",EDGE,"E37.trimOffspring")])]})});
            var Q89;
            Q89=makeQuery(id+"F6.boolean.opBoolean","COPY",EDGE,{"derivedFrom":makeQuery(id+"F6.opExtrude","SWEPT_EDGE",EDGE,{"disambiguationData":[OSD([sQuery(id+"F4.wireOp",EDGE,"E24"),sQuery(id+"F4.wireOp",EDGE,"E37.trimOffspring")])]})});
            var Q90;
            Q90=makeQuery(id+"F5.boolean.opBoolean","COPY",EDGE,{"derivedFrom":makeQuery(id+"F5.opExtrude","SWEPT_EDGE",EDGE,{"disambiguationData":[OSD([sQuery(id+"F4.wireOp",EDGE,"E26"),sQuery(id+"F4.wireOp",EDGE,"E38.trimOffspring")])]})});
            var Q91;
            Q91=makeQuery(id+"F6.boolean.opBoolean","COPY",EDGE,{"derivedFrom":makeQuery(id+"F6.opExtrude","SWEPT_EDGE",EDGE,{"disambiguationData":[OSD([sQuery(id+"F4.wireOp",EDGE,"E28"),sQuery(id+"F4.wireOp",EDGE,"E39.trimOffspring")])]})});
            var Q92;
            Q92=makeQuery(id+"F5.boolean.opBoolean","COPY",EDGE,{"derivedFrom":makeQuery(id+"F5.opExtrude","SWEPT_EDGE",EDGE,{"disambiguationData":[OSD([sQuery(id+"F4.wireOp",EDGE,"E16"),sQuery(id+"F4.wireOp",EDGE,"E19")])]})});
            var Q93;
            Q93=makeQuery(id+"F5.boolean.opBoolean","COPY",EDGE,{"derivedFrom":makeQuery(id+"F5.opExtrude","SWEPT_EDGE",EDGE,{"disambiguationData":[OSD([sQuery(id+"F4.wireOp",EDGE,"E25"),sQuery(id+"F4.wireOp",EDGE,"E38.trimOffspring")])]})});
            var Q94;
            Q94=makeQuery(id+"F6.boolean.opBoolean","COPY",EDGE,{"derivedFrom":makeQuery(id+"F6.opExtrude","SWEPT_EDGE",EDGE,{"disambiguationData":[OSD([sQuery(id+"F4.wireOp",EDGE,"E27"),sQuery(id+"F4.wireOp",EDGE,"E39.trimOffspring")])]})});
            var Q95;
            Q95=makeQuery(id+"F5.boolean.opBoolean","COPY",EDGE,{"derivedFrom":makeQuery(id+"F5.opExtrude","SWEPT_EDGE",EDGE,{"disambiguationData":[OSD([sQuery(id+"F4.wireOp",EDGE,"E16"),sQuery(id+"F4.wireOp",EDGE,"E29")])]})});
            fillet(context, id + "F7", {"entities" : qUnion([Q0, Q1, Q2, Q3, Q4, Q5, Q6, Q7, Q8, Q9, Q10, Q11, Q12, Q13, Q14, Q15, Q16, Q17, Q18, Q19, Q20, Q21, Q22, Q23, Q24, Q25, Q26, Q27, Q28, Q29, Q30, Q31, Q32, Q33, Q34, Q35, Q36, Q37, Q38, Q39, Q40, Q41, Q42, Q43, Q44, Q45, Q46, Q47, Q48, Q49, Q50, Q51, Q52, Q53, Q54, Q55, Q56, Q57, Q58, Q59, Q60, Q61, Q62, Q63, Q64, Q65, Q66, Q67, Q68, Q69, Q70, Q71, Q72, Q73, Q74, Q75, Q76, Q77, Q78, Q79, Q80, Q81, Q82, Q83, Q84, Q85, Q86, Q87, Q88, Q89, Q90, Q91, Q92, Q93, Q94, Q95]), "radius" : 2 * mm, "tangentPropagation" : true, "allowEdgeOverflow" : false});
        }
    });
